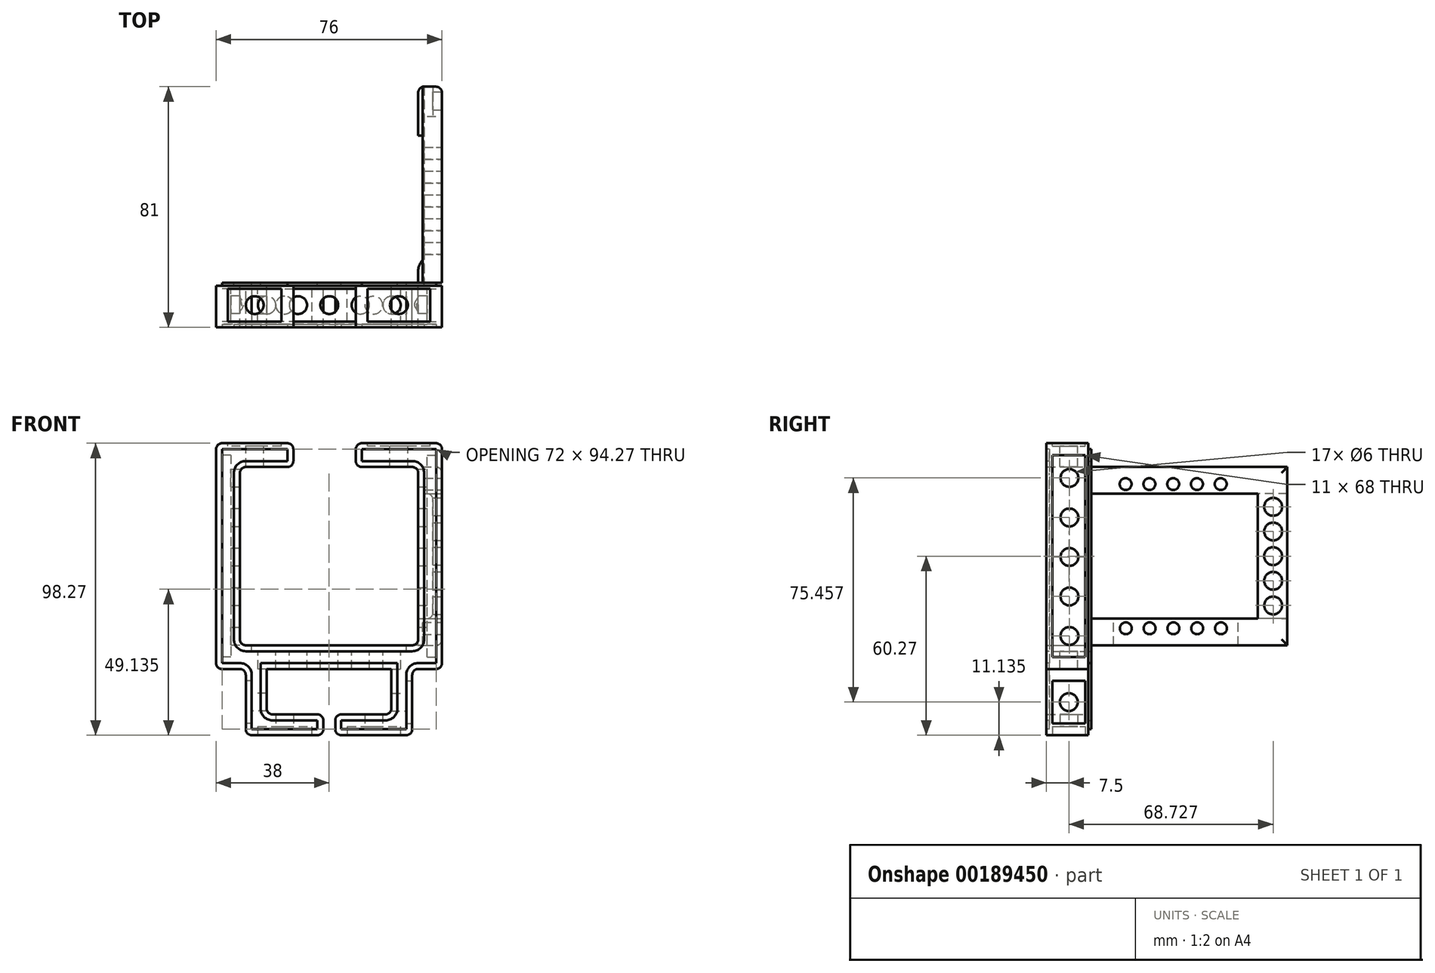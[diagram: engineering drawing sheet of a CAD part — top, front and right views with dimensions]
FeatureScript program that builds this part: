
annotation { "Feature Type Name" : "Feature", "Feature Type Description" : "" }
export const myFeature = defineFeature(function(context is Context, id is Id, definition is map)
    precondition{}
    {
        {
            var Q0;
            Q0=qCreatedBy(makeId("Front.planeOp"),FACE);
            var sketch = newSketch(context, id + "F0", { "sketchPlane" : qUnion([Q0])});
            skLineSegment(sketch, "E0.top", {"start": v(27.9, 40.9) * mm, "end": v(10.9, 40.9) * mm});
            skLineSegment(sketch, "E0.left", {"start": v(29.9, -17.1) * mm, "end": v(29.9, 38.9) * mm});
            skLineSegment(sketch, "E0.right", {"start": v(-30.1, -17.1) * mm, "end": v(-30.1, 38.9) * mm});
            skLineSegment(sketch, "E1.1", {"start": v(37.9, -25.1) * mm, "end": v(37.9, 46.9) * mm});
            skPoint(sketch, "E2.visualSharp", {"position": v(-30.1, -19.1) * mm});
            skArc(sketch, "E2.filletArc", {"start": v(-30.1, -17.1) * mm, "mid": v(-29.51, -18.51) * mm, "end": v(-28.1, -19.1) * mm});
            skPoint(sketch, "E3.visualSharp", {"position": v(29.9, -19.1) * mm});
            skArc(sketch, "E3.filletArc", {"start": v(27.9, -19.1) * mm, "mid": v(29.31, -18.51) * mm, "end": v(29.9, -17.1) * mm});
            skPoint(sketch, "E4.visualSharp", {"position": v(-30.1, 40.9) * mm});
            skArc(sketch, "E4.filletArc", {"start": v(-28.1, 40.9) * mm, "mid": v(-29.51, 40.31) * mm, "end": v(-30.1, 38.9) * mm});
            skPoint(sketch, "E5.visualSharp", {"position": v(29.9, 40.9) * mm});
            skArc(sketch, "E5.filletArc", {"start": v(29.9, 38.9) * mm, "mid": v(29.31, 40.31) * mm, "end": v(27.9, 40.9) * mm});
            skPoint(sketch, "E6.visualSharp", {"position": v(-38.1, 48.9) * mm});
            skArc(sketch, "E6.filletArc", {"start": v(-36.1, 48.9) * mm, "mid": v(-37.51, 48.31) * mm, "end": v(-38.1, 46.9) * mm});
            skPoint(sketch, "E7.visualSharp", {"position": v(37.9, 48.9) * mm});
            skArc(sketch, "E7.filletArc", {"start": v(37.9, 46.9) * mm, "mid": v(37.31, 48.31) * mm, "end": v(35.9, 48.9) * mm});
            skPoint(sketch, "E8.visualSharp", {"position": v(37.9, -27.1) * mm});
            skArc(sketch, "E8.filletArc", {"start": v(35.9, -27.1) * mm, "mid": v(37.31, -26.51) * mm, "end": v(37.9, -25.1) * mm});
            skPoint(sketch, "E9.visualSharp", {"position": v(-29.82, -12.89) * mm});
            skLineSegment(sketch, "E10", {"start": v(-28.1, -19.1) * mm, "end": v(27.9, -19.1) * mm});
            skLineSegment(sketch, "E11", {"start": v(-38.1, 46.9) * mm, "end": v(-38.1, -25.1) * mm});
            skLineSegment(sketch, "E12", {"start": v(-36.1, -27.1) * mm, "end": v(-30.1, -27.1) * mm});
            skLineSegment(sketch, "E13.bottom", {"start": v(-21.1, -27.1) * mm, "end": v(20.9, -27.1) * mm});
            skLineSegment(sketch, "E13.top", {"start": v(-26.1, -49.37) * mm, "end": v(-4, -49.37) * mm});
            skLineSegment(sketch, "E14", {"start": v(-28.1, -29.1) * mm, "end": v(-28.1, -47.37) * mm});
            skLineSegment(sketch, "E15", {"start": v(27.9, -47.37) * mm, "end": v(27.9, -29.1) * mm});
            skLineSegment(sketch, "E16", {"start": v(-19.1, -42.37) * mm, "end": v(-4, -42.37) * mm});
            skLineSegment(sketch, "E17", {"start": v(4, -42.37) * mm, "end": v(18.9, -42.37) * mm});
            skLineSegment(sketch, "E18", {"start": v(-2, -44.37) * mm, "end": v(-2, -47.37) * mm});
            skLineSegment(sketch, "E19", {"start": v(2, -44.37) * mm, "end": v(2, -47.37) * mm});
            skPoint(sketch, "E20.visualSharp", {"position": v(20.9, -42.37) * mm});
            skArc(sketch, "E20.filletArc", {"start": v(18.9, -42.37) * mm, "mid": v(20.31, -41.78) * mm, "end": v(20.9, -40.37) * mm});
            skPoint(sketch, "E21.visualSharp", {"position": v(-21.1, -42.37) * mm});
            skArc(sketch, "E21.filletArc", {"start": v(-21.1, -40.37) * mm, "mid": v(-20.51, -41.78) * mm, "end": v(-19.1, -42.37) * mm});
            skPoint(sketch, "E22.visualSharp", {"position": v(27.9, -49.37) * mm});
            skArc(sketch, "E22.filletArc", {"start": v(25.9, -49.37) * mm, "mid": v(27.31, -48.78) * mm, "end": v(27.9, -47.37) * mm});
            skPoint(sketch, "E23.visualSharp", {"position": v(-28.1, -49.37) * mm});
            skArc(sketch, "E23.filletArc", {"start": v(-28.1, -47.37) * mm, "mid": v(-27.51, -48.78) * mm, "end": v(-26.1, -49.37) * mm});
            skLineSegment(sketch, "E24.trimOffspring", {"start": v(29.9, -27.1) * mm, "end": v(35.9, -27.1) * mm});
            skPoint(sketch, "E25.visualSharp", {"position": v(27.9, -27.1) * mm});
            skArc(sketch, "E25.filletArc", {"start": v(29.9, -27.1) * mm, "mid": v(28.49, -27.69) * mm, "end": v(27.9, -29.1) * mm});
            skPoint(sketch, "E26.visualSharp", {"position": v(-28.1, -27.1) * mm});
            skArc(sketch, "E26.filletArc", {"start": v(-28.1, -29.1) * mm, "mid": v(-28.69, -27.69) * mm, "end": v(-30.1, -27.1) * mm});
            skPoint(sketch, "E27.visualSharp", {"position": v(-38.1, -27.1) * mm});
            skArc(sketch, "E27.filletArc", {"start": v(-38.1, -25.1) * mm, "mid": v(-37.51, -26.51) * mm, "end": v(-36.1, -27.1) * mm});
            skLineSegment(sketch, "E28", {"start": v(-21.1, -27.1) * mm, "end": v(-21.1, -40.37) * mm});
            skLineSegment(sketch, "E29", {"start": v(20.9, -27.1) * mm, "end": v(20.9, -40.37) * mm});
            skLineSegment(sketch, "E30.trimOffspring", {"start": v(4, -49.37) * mm, "end": v(25.9, -49.37) * mm});
            skPoint(sketch, "E31.start.orphan", {"position": v(0, -42.37) * mm});
            skPoint(sketch, "E32.visualSharp", {"position": v(-2, -42.37) * mm});
            skArc(sketch, "E32.filletArc", {"start": v(-2, -44.37) * mm, "mid": v(-2.59, -42.95) * mm, "end": v(-4, -42.37) * mm});
            skPoint(sketch, "E33.visualSharp", {"position": v(2, -42.37) * mm});
            skArc(sketch, "E33.filletArc", {"start": v(4, -42.37) * mm, "mid": v(2.59, -42.95) * mm, "end": v(2, -44.37) * mm});
            skPoint(sketch, "E34.visualSharp", {"position": v(2, -49.37) * mm});
            skArc(sketch, "E34.filletArc", {"start": v(2, -47.37) * mm, "mid": v(2.59, -48.78) * mm, "end": v(4, -49.37) * mm});
            skPoint(sketch, "E35.visualSharp", {"position": v(-2, -49.37) * mm});
            skArc(sketch, "E35.filletArc", {"start": v(-4, -49.37) * mm, "mid": v(-2.59, -48.78) * mm, "end": v(-2, -47.37) * mm});
            skLineSegment(sketch, "E36", {"start": v(27.9, -27.1) * mm, "end": v(27.9, -29.1) * mm});
            skLineSegment(sketch, "E37", {"start": v(-28.1, -19.1) * mm, "end": v(-28.1, -29.1) * mm});
            skLineSegment(sketch, "E38", {"start": v(29.9, -17.1) * mm, "end": v(29.9, -27.1) * mm});
            skLineSegment(sketch, "E39", {"start": v(-12.1, 46.9) * mm, "end": v(-12.1, 42.9) * mm});
            skLineSegment(sketch, "E40", {"start": v(8.9, 46.9) * mm, "end": v(8.9, 42.9) * mm});
            skLineSegment(sketch, "E41.trimOffspring", {"start": v(-14.1, 40.9) * mm, "end": v(-28.1, 40.9) * mm});
            skPoint(sketch, "E42.end.orphan", {"position": v(-0.1, 40.9) * mm});
            skPoint(sketch, "E43.orphan", {"position": v(-0.1, 48.9) * mm});
            skPoint(sketch, "E44.visualSharp", {"position": v(-12.1, 40.9) * mm});
            skArc(sketch, "E44.filletArc", {"start": v(-14.1, 40.9) * mm, "mid": v(-12.69, 41.49) * mm, "end": v(-12.1, 42.9) * mm});
            skPoint(sketch, "E45.visualSharp", {"position": v(8.9, 40.9) * mm});
            skArc(sketch, "E45.filletArc", {"start": v(8.9, 42.9) * mm, "mid": v(9.49, 41.49) * mm, "end": v(10.9, 40.9) * mm});
            skPoint(sketch, "E46.start.orphan", {"position": v(-18.1, 48.9) * mm});
            skPoint(sketch, "E47.start.orphan", {"position": v(17.9, 48.9) * mm});
            skLineSegment(sketch, "E48", {"start": v(-36.1, 48.9) * mm, "end": v(-14.1, 48.9) * mm});
            skLineSegment(sketch, "E49", {"start": v(10.9, 48.9) * mm, "end": v(35.9, 48.9) * mm});
            skPoint(sketch, "E50.visualSharp", {"position": v(-12.1, 48.9) * mm});
            skArc(sketch, "E50.filletArc", {"start": v(-12.1, 46.9) * mm, "mid": v(-12.69, 48.31) * mm, "end": v(-14.1, 48.9) * mm});
            skPoint(sketch, "E51.visualSharp", {"position": v(8.9, 48.9) * mm});
            skArc(sketch, "E51.filletArc", {"start": v(10.9, 48.9) * mm, "mid": v(9.49, 48.31) * mm, "end": v(8.9, 46.9) * mm});
            skSolve(sketch);
        }
        {
            var Q0;
            Q0=makeQuery(id+"F0.imprint","IMPRINT",FACE,{"disambiguationData":[TD([[makeQuery(id+"F0.imprint","IMPRINT",EDGE,{"derivedFrom":sQuery(id+"F0.wireOp",EDGE,"E0.left")}),-1.0]])]});
            var Q1;
            Q1=makeQuery(id+"F0.imprint","IMPRINT",FACE,{"disambiguationData":[TD([[makeQuery(id+"F0.imprint","IMPRINT",EDGE,{"derivedFrom":sQuery(id+"F0.wireOp",EDGE,"E0.right")}),1.0]])]});
            var Q2;
            Q2=makeQuery(id+"F0.imprint","IMPRINT",FACE,{"disambiguationData":[TD([[makeQuery(id+"F0.imprint","IMPRINT",EDGE,{"derivedFrom":sQuery(id+"F0.wireOp",EDGE,"E10")}),-1.0]])]});
            var Q3;
            {var subQ0=sQuery(id+"F0.wireOp",EDGE,"iEe1PrU2-Olpx-yFy5-rcaY-dY1r3bGIUNjf");Q3=makeQuery(id+"F0.imprint","IMPRINT",FACE,{"disambiguationData":[TD([[makeQuery(id+"F0.imprint","IMPRINT",EDGE,{"derivedFrom":subQ0}),1.0]])]});}
            var Q4;
            {var subQ0=sQuery(id+"F0.wireOp",EDGE,"4XO8oygt-JLlM-bsj2-xD9l-5jJy744JPbBX");Q4=makeQuery(id+"F0.imprint","IMPRINT",FACE,{"disambiguationData":[TD([[makeQuery(id+"F0.imprint","IMPRINT",EDGE,{"derivedFrom":subQ0}),-1.0]])]});}
            extrude(context, id + "F1", {"entities" : qUnion([Q0, Q1, Q2, Q3, Q4]), "depth" : 15 * mm});
        }
        {
            var Q0;
            Q0=makeQuery(id+"F1.opExtrude","SWEPT_FACE",FACE,{"disambiguationData":[OSD([sQuery(id+"F0.wireOp",EDGE,"E11")])]});
            var sketch = newSketch(context, id + "F2", { "sketchPlane" : qUnion([Q0])});
            skLineSegment(sketch, "E52.0", {"start": v(2, 44.9) * mm, "end": v(2, -23.1) * mm});
            skLineSegment(sketch, "E52.1", {"start": v(13, 44.9) * mm, "end": v(2, 44.9) * mm});
            skLineSegment(sketch, "E52.2", {"start": v(13, -23.1) * mm, "end": v(13, 44.9) * mm});
            skLineSegment(sketch, "E52.3", {"start": v(2, -23.1) * mm, "end": v(13, -23.1) * mm});
            skSolve(sketch);
        }
        {
            var Q0;
            Q0=makeQuery(id+"F2.imprint","IMPRINT",FACE,{"disambiguationData":[TD([[makeQuery(id+"F2.imprint","IMPRINT",EDGE,{"derivedFrom":sQuery(id+"F2.wireOp",EDGE,"E52.0")}),1.0]])]});
            extrude(context, id + "F3", {"entities" : qUnion([Q0]), "operationType" : NewBodyOperationType.REMOVE, "oppositeDirection" : true, "depth" : 5 * mm});
        }
        {
            var Q0;
            Q0=makeQuery(id+"F1.opExtrude","SWEPT_FACE",FACE,{"disambiguationData":[OSD([sQuery(id+"F0.wireOp",EDGE,"E1.1")])]});
            var sketch = newSketch(context, id + "F4", { "sketchPlane" : qUnion([Q0])});
            skLineSegment(sketch, "E53.0", {"start": v(-2, -23.1) * mm, "end": v(-2, 44.9) * mm});
            skLineSegment(sketch, "E53.1", {"start": v(-13, -23.1) * mm, "end": v(-2, -23.1) * mm});
            skLineSegment(sketch, "E53.2", {"start": v(-13, 44.9) * mm, "end": v(-13, -23.1) * mm});
            skLineSegment(sketch, "E53.3", {"start": v(-2, 44.9) * mm, "end": v(-13, 44.9) * mm});
            skCircle(sketch, "E54", {"center": v(-7.3, 37.22) * mm, "radius": 3 * mm});
            skCircle(sketch, "E55.0.1.0", {"center": v(-7.3, 23.92) * mm, "radius": 3 * mm});
            skCircle(sketch, "E55.0.2.0", {"center": v(-7.3, 10.62) * mm, "radius": 3 * mm});
            skCircle(sketch, "E55.0.3.0", {"center": v(-7.3, -2.68) * mm, "radius": 3 * mm});
            skCircle(sketch, "E55.0.4.0", {"center": v(-7.3, -15.98) * mm, "radius": 3 * mm});
            skLineSegment(sketch, "E55.direction1", {"start": v(-7.8, 37.22) * mm, "end": v(17.2, 37.22) * mm, "construction": true});
            skLineSegment(sketch, "E55.direction2", {"start": v(-7.8, 37.22) * mm, "end": v(-7.8, 23.92) * mm, "construction": true});
            skSolve(sketch);
        }
        {
            var Q0;
            Q0=makeQuery(id+"F4.imprint","IMPRINT",FACE,{"disambiguationData":[TD([[makeQuery(id+"F4.imprint","IMPRINT",EDGE,{"derivedFrom":sQuery(id+"F4.wireOp",EDGE,"E54")}),1.0]])]});
            var Q1;
            Q1=makeQuery(id+"F4.imprint","IMPRINT",FACE,{"disambiguationData":[TD([[makeQuery(id+"F4.imprint","IMPRINT",EDGE,{"derivedFrom":sQuery(id+"F4.wireOp",EDGE,"E55.0.1.0")}),1.0]])]});
            var Q2;
            Q2=makeQuery(id+"F4.imprint","IMPRINT",FACE,{"disambiguationData":[TD([[makeQuery(id+"F4.imprint","IMPRINT",EDGE,{"derivedFrom":sQuery(id+"F4.wireOp",EDGE,"E55.0.2.0")}),1.0]])]});
            var Q3;
            Q3=makeQuery(id+"F4.imprint","IMPRINT",FACE,{"disambiguationData":[TD([[makeQuery(id+"F4.imprint","IMPRINT",EDGE,{"derivedFrom":sQuery(id+"F4.wireOp",EDGE,"E55.0.3.0")}),1.0]])]});
            var Q4;
            Q4=makeQuery(id+"F4.imprint","IMPRINT",FACE,{"disambiguationData":[TD([[makeQuery(id+"F4.imprint","IMPRINT",EDGE,{"derivedFrom":sQuery(id+"F4.wireOp",EDGE,"E55.0.4.0")}),1.0]])]});
            extrude(context, id + "F5", {"entities" : qUnion([Q0, Q1, Q2, Q3, Q4]), "operationType" : NewBodyOperationType.REMOVE, "oppositeDirection" : true, "depth" : 90.3 * mm});
        }
        {
            var Q0;
            Q0=makeQuery(id+"F4.imprint","IMPRINT",FACE,{"disambiguationData":[TD([[makeQuery(id+"F4.imprint","IMPRINT",EDGE,{"derivedFrom":sQuery(id+"F4.wireOp",EDGE,"E53.0")}),1.0]])]});
            extrude(context, id + "F6", {"entities" : qUnion([Q0]), "operationType" : NewBodyOperationType.REMOVE, "oppositeDirection" : true, "depth" : 5 * mm});
        }
        {
            var Q0;
            Q0=makeQuery(id+"F1.opExtrude","CAP_FACE",FACE,{"disambiguationData":[OSD([sQuery(id+"F0.wireOp",EDGE,"E0.top"),sQuery(id+"F0.wireOp",EDGE,"E0.left"),sQuery(id+"F0.wireOp",EDGE,"E0.right"),sQuery(id+"F0.wireOp",EDGE,"E1.0"),sQuery(id+"F0.wireOp",EDGE,"E1.1"),sQuery(id+"F0.wireOp",EDGE,"E2.filletArc"),sQuery(id+"F0.wireOp",EDGE,"E3.filletArc"),sQuery(id+"F0.wireOp",EDGE,"E4.filletArc"),sQuery(id+"F0.wireOp",EDGE,"E5.filletArc"),sQuery(id+"F0.wireOp",EDGE,"E6.filletArc"),sQuery(id+"F0.wireOp",EDGE,"E7.filletArc"),sQuery(id+"F0.wireOp",EDGE,"E8.filletArc"),sQuery(id+"F0.wireOp",EDGE,"XpEmfxVq-F5ly-u82n-WrmS-VlENYUEvmkYp"),sQuery(id+"F0.wireOp",EDGE,"E10"),sQuery(id+"F0.wireOp",EDGE,"E11"),sQuery(id+"F0.wireOp",EDGE,"E12"),sQuery(id+"F0.wireOp",EDGE,"E13.top"),sQuery(id+"F0.wireOp",EDGE,"E14"),sQuery(id+"F0.wireOp",EDGE,"E15"),sQuery(id+"F0.wireOp",EDGE,"E16"),sQuery(id+"F0.wireOp",EDGE,"E17"),sQuery(id+"F0.wireOp",EDGE,"E18"),sQuery(id+"F0.wireOp",EDGE,"E19"),sQuery(id+"F0.wireOp",EDGE,"E20.filletArc"),sQuery(id+"F0.wireOp",EDGE,"E21.filletArc"),sQuery(id+"F0.wireOp",EDGE,"E22.filletArc"),sQuery(id+"F0.wireOp",EDGE,"E23.filletArc"),sQuery(id+"F0.wireOp",EDGE,"E13.bottom"),sQuery(id+"F0.wireOp",EDGE,"E24.trimOffspring"),sQuery(id+"F0.wireOp",EDGE,"E25.filletArc"),sQuery(id+"F0.wireOp",EDGE,"E26.filletArc"),sQuery(id+"F0.wireOp",EDGE,"E27.filletArc"),sQuery(id+"F0.wireOp",EDGE,"E28"),sQuery(id+"F0.wireOp",EDGE,"E29"),sQuery(id+"F0.wireOp",EDGE,"E30.trimOffspring"),sQuery(id+"F0.wireOp",EDGE,"E32.filletArc"),sQuery(id+"F0.wireOp",EDGE,"E33.filletArc"),sQuery(id+"F0.wireOp",EDGE,"E34.filletArc"),sQuery(id+"F0.wireOp",EDGE,"E35.filletArc"),sQuery(id+"F0.wireOp",EDGE,"E46"),sQuery(id+"F0.wireOp",EDGE,"E47"),sQuery(id+"F0.wireOp",EDGE,"E39"),sQuery(id+"F0.wireOp",EDGE,"E40")])],"isStart":false});
            var sketch = newSketch(context, id + "F7", { "sketchPlane" : qUnion([Q0])});
            skLineSegment(sketch, "E56.0", {"start": v(10.9, 46.9) * mm, "end": v(10.9, 42.9) * mm});
            skLineSegment(sketch, "E56.1", {"start": v(35.9, 46.9) * mm, "end": v(10.9, 46.9) * mm});
            skLineSegment(sketch, "E56.2", {"start": v(35.9, -25.1) * mm, "end": v(35.9, 46.9) * mm});
            skLineSegment(sketch, "E56.3", {"start": v(29.9, -25.1) * mm, "end": v(35.9, -25.1) * mm});
            skArc(sketch, "E56.4", {"start": v(25.9, -29.1) * mm, "mid": v(27.07, -26.27) * mm, "end": v(29.9, -25.1) * mm});
            skLineSegment(sketch, "E56.5", {"start": v(25.9, -47.37) * mm, "end": v(25.9, -29.1) * mm});
            skLineSegment(sketch, "E56.6", {"start": v(4, -47.37) * mm, "end": v(25.9, -47.37) * mm});
            skLineSegment(sketch, "E56.7", {"start": v(4, -44.37) * mm, "end": v(4, -47.37) * mm});
            skLineSegment(sketch, "E56.8", {"start": v(18.9, -44.37) * mm, "end": v(4, -44.37) * mm});
            skLineSegment(sketch, "E56.9", {"start": v(-14.1, 46.9) * mm, "end": v(-36.1, 46.9) * mm});
            skLineSegment(sketch, "E56.10", {"start": v(-14.1, 42.9) * mm, "end": v(-14.1, 46.9) * mm});
            skLineSegment(sketch, "E56.11", {"start": v(-28.1, 42.9) * mm, "end": v(-14.1, 42.9) * mm});
            skArc(sketch, "E56.12", {"start": v(-32.1, 38.9) * mm, "mid": v(-30.93, 41.73) * mm, "end": v(-28.1, 42.9) * mm});
            skLineSegment(sketch, "E56.13", {"start": v(-32.1, -17.1) * mm, "end": v(-32.1, 38.9) * mm});
            skArc(sketch, "E56.14", {"start": v(-28.1, -21.1) * mm, "mid": v(-30.93, -19.93) * mm, "end": v(-32.1, -17.1) * mm});
            skArc(sketch, "E56.15", {"start": v(27.9, 42.9) * mm, "mid": v(30.73, 41.73) * mm, "end": v(31.9, 38.9) * mm});
            skLineSegment(sketch, "E56.16", {"start": v(31.9, 38.9) * mm, "end": v(31.9, -17.1) * mm});
            skArc(sketch, "E56.17", {"start": v(31.9, -17.1) * mm, "mid": v(30.73, -19.93) * mm, "end": v(27.9, -21.1) * mm});
            skLineSegment(sketch, "E56.18", {"start": v(27.9, -21.1) * mm, "end": v(-28.1, -21.1) * mm});
            skLineSegment(sketch, "E56.19", {"start": v(-36.1, 46.9) * mm, "end": v(-36.1, -25.1) * mm});
            skLineSegment(sketch, "E56.20", {"start": v(-36.1, -25.1) * mm, "end": v(-30.1, -25.1) * mm});
            skArc(sketch, "E56.21", {"start": v(-30.1, -25.1) * mm, "mid": v(-27.27, -26.27) * mm, "end": v(-26.1, -29.1) * mm});
            skLineSegment(sketch, "E56.22", {"start": v(-26.1, -29.1) * mm, "end": v(-26.1, -47.37) * mm});
            skLineSegment(sketch, "E56.23", {"start": v(-26.1, -47.37) * mm, "end": v(-4, -47.37) * mm});
            skLineSegment(sketch, "E56.24", {"start": v(-4, -47.37) * mm, "end": v(-4, -44.37) * mm});
            skLineSegment(sketch, "E56.25", {"start": v(-4, -44.37) * mm, "end": v(-19.1, -44.37) * mm});
            skArc(sketch, "E56.26", {"start": v(-19.1, -44.37) * mm, "mid": v(-21.93, -43.2) * mm, "end": v(-23.1, -40.37) * mm});
            skLineSegment(sketch, "E56.27", {"start": v(-23.1, -40.37) * mm, "end": v(-23.1, -25.1) * mm});
            skLineSegment(sketch, "E56.28", {"start": v(10.9, 42.9) * mm, "end": v(27.9, 42.9) * mm});
            skLineSegment(sketch, "E56.29", {"start": v(-23.1, -25.1) * mm, "end": v(22.9, -25.1) * mm});
            skLineSegment(sketch, "E56.30", {"start": v(22.9, -25.1) * mm, "end": v(22.9, -40.37) * mm});
            skArc(sketch, "E56.31", {"start": v(22.9, -40.37) * mm, "mid": v(21.73, -43.2) * mm, "end": v(18.9, -44.37) * mm});
            skSolve(sketch);
        }
        {
            var Q0;
            Q0=makeQuery(id+"F7.imprint","IMPRINT",FACE,{"disambiguationData":[TD([[makeQuery(id+"F7.imprint","IMPRINT",EDGE,{"derivedFrom":sQuery(id+"F7.wireOp",EDGE,"E56.0")}),1.0]])]});
            extrude(context, id + "F8", {"entities" : qUnion([Q0]), "operationType" : NewBodyOperationType.REMOVE, "oppositeDirection" : true, "depth" : 1 * mm});
        }
        {
            var Q0;
            Q0=makeQuery(id+"F1.opExtrude","CAP_FACE",FACE,{"disambiguationData":[OSD([sQuery(id+"F0.wireOp",EDGE,"E0.top"),sQuery(id+"F0.wireOp",EDGE,"E0.left"),sQuery(id+"F0.wireOp",EDGE,"E0.right"),sQuery(id+"F0.wireOp",EDGE,"E1.0"),sQuery(id+"F0.wireOp",EDGE,"E1.1"),sQuery(id+"F0.wireOp",EDGE,"E2.filletArc"),sQuery(id+"F0.wireOp",EDGE,"E3.filletArc"),sQuery(id+"F0.wireOp",EDGE,"E4.filletArc"),sQuery(id+"F0.wireOp",EDGE,"E5.filletArc"),sQuery(id+"F0.wireOp",EDGE,"E6.filletArc"),sQuery(id+"F0.wireOp",EDGE,"E7.filletArc"),sQuery(id+"F0.wireOp",EDGE,"E8.filletArc"),sQuery(id+"F0.wireOp",EDGE,"XpEmfxVq-F5ly-u82n-WrmS-VlENYUEvmkYp"),sQuery(id+"F0.wireOp",EDGE,"E10"),sQuery(id+"F0.wireOp",EDGE,"E11"),sQuery(id+"F0.wireOp",EDGE,"E12"),sQuery(id+"F0.wireOp",EDGE,"E13.top"),sQuery(id+"F0.wireOp",EDGE,"E14"),sQuery(id+"F0.wireOp",EDGE,"E15"),sQuery(id+"F0.wireOp",EDGE,"E16"),sQuery(id+"F0.wireOp",EDGE,"E17"),sQuery(id+"F0.wireOp",EDGE,"E18"),sQuery(id+"F0.wireOp",EDGE,"E19"),sQuery(id+"F0.wireOp",EDGE,"E20.filletArc"),sQuery(id+"F0.wireOp",EDGE,"E21.filletArc"),sQuery(id+"F0.wireOp",EDGE,"E22.filletArc"),sQuery(id+"F0.wireOp",EDGE,"E23.filletArc"),sQuery(id+"F0.wireOp",EDGE,"E13.bottom"),sQuery(id+"F0.wireOp",EDGE,"E24.trimOffspring"),sQuery(id+"F0.wireOp",EDGE,"E25.filletArc"),sQuery(id+"F0.wireOp",EDGE,"E26.filletArc"),sQuery(id+"F0.wireOp",EDGE,"E27.filletArc"),sQuery(id+"F0.wireOp",EDGE,"E28"),sQuery(id+"F0.wireOp",EDGE,"E29"),sQuery(id+"F0.wireOp",EDGE,"E30.trimOffspring"),sQuery(id+"F0.wireOp",EDGE,"E32.filletArc"),sQuery(id+"F0.wireOp",EDGE,"E33.filletArc"),sQuery(id+"F0.wireOp",EDGE,"E34.filletArc"),sQuery(id+"F0.wireOp",EDGE,"E35.filletArc"),sQuery(id+"F0.wireOp",EDGE,"E46"),sQuery(id+"F0.wireOp",EDGE,"E47"),sQuery(id+"F0.wireOp",EDGE,"E39"),sQuery(id+"F0.wireOp",EDGE,"E40")])],"isStart":true});
            var sketch = newSketch(context, id + "F9", { "sketchPlane" : qUnion([Q0])});
            skArc(sketch, "E57.0", {"start": v(-31.9, 38.9) * mm, "mid": v(-30.73, 41.73) * mm, "end": v(-27.9, 42.9) * mm});
            skLineSegment(sketch, "E57.1", {"start": v(-31.9, -17.1) * mm, "end": v(-31.9, 38.9) * mm});
            skArc(sketch, "E57.2", {"start": v(-27.9, -21.1) * mm, "mid": v(-30.73, -19.93) * mm, "end": v(-31.9, -17.1) * mm});
            skLineSegment(sketch, "E57.3", {"start": v(28.1, -21.1) * mm, "end": v(-27.9, -21.1) * mm});
            skArc(sketch, "E57.4", {"start": v(32.1, -17.1) * mm, "mid": v(30.93, -19.93) * mm, "end": v(28.1, -21.1) * mm});
            skLineSegment(sketch, "E57.5", {"start": v(32.1, 38.9) * mm, "end": v(32.1, -17.1) * mm});
            skArc(sketch, "E57.6", {"start": v(28.1, 42.9) * mm, "mid": v(30.93, 41.73) * mm, "end": v(32.1, 38.9) * mm});
            skLineSegment(sketch, "E57.7", {"start": v(14.1, 42.9) * mm, "end": v(28.1, 42.9) * mm});
            skLineSegment(sketch, "E57.8", {"start": v(14.1, 46.9) * mm, "end": v(14.1, 42.9) * mm});
            skArc(sketch, "E57.9", {"start": v(-18.9, -44.37) * mm, "mid": v(-21.73, -43.2) * mm, "end": v(-22.9, -40.37) * mm});
            skLineSegment(sketch, "E57.10", {"start": v(-4, -44.37) * mm, "end": v(-18.9, -44.37) * mm});
            skLineSegment(sketch, "E57.11", {"start": v(-4, -47.37) * mm, "end": v(-4, -44.37) * mm});
            skLineSegment(sketch, "E57.12", {"start": v(-25.9, -47.37) * mm, "end": v(-4, -47.37) * mm});
            skLineSegment(sketch, "E57.13", {"start": v(-25.9, -29.1) * mm, "end": v(-25.9, -47.37) * mm});
            skArc(sketch, "E57.14", {"start": v(-29.9, -25.1) * mm, "mid": v(-27.07, -26.27) * mm, "end": v(-25.9, -29.1) * mm});
            skLineSegment(sketch, "E57.15", {"start": v(-10.9, 42.9) * mm, "end": v(-10.9, 46.9) * mm});
            skLineSegment(sketch, "E57.16", {"start": v(-10.9, 46.9) * mm, "end": v(-35.9, 46.9) * mm});
            skLineSegment(sketch, "E57.17", {"start": v(-35.9, 46.9) * mm, "end": v(-35.9, -25.1) * mm});
            skLineSegment(sketch, "E57.18", {"start": v(-35.9, -25.1) * mm, "end": v(-29.9, -25.1) * mm});
            skLineSegment(sketch, "E57.19", {"start": v(-22.9, -40.37) * mm, "end": v(-22.9, -25.1) * mm});
            skLineSegment(sketch, "E57.20", {"start": v(-22.9, -25.1) * mm, "end": v(23.1, -25.1) * mm});
            skLineSegment(sketch, "E57.21", {"start": v(23.1, -25.1) * mm, "end": v(23.1, -40.37) * mm});
            skArc(sketch, "E57.22", {"start": v(23.1, -40.37) * mm, "mid": v(21.93, -43.2) * mm, "end": v(19.1, -44.37) * mm});
            skLineSegment(sketch, "E57.23", {"start": v(19.1, -44.37) * mm, "end": v(4, -44.37) * mm});
            skLineSegment(sketch, "E57.24", {"start": v(4, -44.37) * mm, "end": v(4, -47.37) * mm});
            skLineSegment(sketch, "E57.25", {"start": v(4, -47.37) * mm, "end": v(26.1, -47.37) * mm});
            skLineSegment(sketch, "E57.26", {"start": v(26.1, -47.37) * mm, "end": v(26.1, -29.1) * mm});
            skArc(sketch, "E57.27", {"start": v(26.1, -29.1) * mm, "mid": v(27.27, -26.27) * mm, "end": v(30.1, -25.1) * mm});
            skLineSegment(sketch, "E57.28", {"start": v(-27.9, 42.9) * mm, "end": v(-10.9, 42.9) * mm});
            skLineSegment(sketch, "E57.29", {"start": v(30.1, -25.1) * mm, "end": v(36.1, -25.1) * mm});
            skLineSegment(sketch, "E57.30", {"start": v(36.1, -25.1) * mm, "end": v(36.1, 46.9) * mm});
            skLineSegment(sketch, "E57.31", {"start": v(36.1, 46.9) * mm, "end": v(14.1, 46.9) * mm});
            skSolve(sketch);
        }
        {
            var Q0;
            Q0=makeQuery(id+"F9.imprint","IMPRINT",FACE,{"disambiguationData":[TD([[makeQuery(id+"F9.imprint","IMPRINT",EDGE,{"derivedFrom":sQuery(id+"F9.wireOp",EDGE,"E57.0")}),1.0]])]});
            extrude(context, id + "F10", {"entities" : qUnion([Q0]), "operationType" : NewBodyOperationType.REMOVE, "oppositeDirection" : true, "depth" : 1 * mm});
        }
        {
            var Q0;
            Q0=makeQuery(id+"F1.opExtrude","SWEPT_FACE",FACE,{"disambiguationData":[OSD([sQuery(id+"F0.wireOp",EDGE,"E10")])]});
            var sketch = newSketch(context, id + "F11", { "sketchPlane" : qUnion([Q0])});
            skLineSegment(sketch, "E58.0", {"start": v(25.9, -2) * mm, "end": v(-26.1, -2) * mm});
            skLineSegment(sketch, "E58.1", {"start": v(25.9, -13) * mm, "end": v(25.9, -2) * mm});
            skLineSegment(sketch, "E58.2", {"start": v(-26.1, -13) * mm, "end": v(25.9, -13) * mm});
            skLineSegment(sketch, "E58.3", {"start": v(-26.1, -2) * mm, "end": v(-26.1, -13) * mm});
            skCircle(sketch, "E59", {"center": v(0, -7.5) * mm, "radius": 3 * mm});
            skPoint(sketch, "E59.centerSnap0", {"position": v(25.9, -7.5) * mm});
            skCircle(sketch, "E60", {"center": v(-26.1, -46.3) * mm, "radius": 6.5 * mm});
            skPoint(sketch, "E60.centerSnap0", {"position": v(-26.1, -7.5) * mm});
            skCircle(sketch, "E61.1.0.0", {"center": v(10.5, -7.5) * mm, "radius": 3 * mm});
            skCircle(sketch, "E61.2.0.0", {"center": v(21, -7.5) * mm, "radius": 3 * mm});
            skLineSegment(sketch, "E61.direction1", {"start": v(0, -7.5) * mm, "end": v(10.5, -7.5) * mm, "construction": true});
            skCircle(sketch, "E62.1.0.0", {"center": v(-10.5, -7.5) * mm, "radius": 3 * mm});
            skCircle(sketch, "E62.2.0.0", {"center": v(-21, -7.5) * mm, "radius": 3 * mm});
            skLineSegment(sketch, "E62.direction1", {"start": v(0, -7.5) * mm, "end": v(-10.5, -7.5) * mm, "construction": true});
            skSolve(sketch);
        }
        {
            var Q0;
            Q0=makeQuery(id+"F11.imprint","IMPRINT",FACE,{"disambiguationData":[TD([[makeQuery(id+"F11.imprint","IMPRINT",EDGE,{"derivedFrom":sQuery(id+"F11.wireOp",EDGE,"E61.2.0.0")}),1.0]])]});
            var Q1;
            Q1=makeQuery(id+"F11.imprint","IMPRINT",FACE,{"disambiguationData":[TD([[makeQuery(id+"F11.imprint","IMPRINT",EDGE,{"derivedFrom":sQuery(id+"F11.wireOp",EDGE,"E61.1.0.0")}),1.0]])]});
            var Q2;
            Q2=makeQuery(id+"F11.imprint","IMPRINT",FACE,{"disambiguationData":[TD([[makeQuery(id+"F11.imprint","IMPRINT",EDGE,{"derivedFrom":sQuery(id+"F11.wireOp",EDGE,"E59")}),1.0]])]});
            var Q3;
            Q3=makeQuery(id+"F11.imprint","IMPRINT",FACE,{"disambiguationData":[TD([[makeQuery(id+"F11.imprint","IMPRINT",EDGE,{"derivedFrom":sQuery(id+"F11.wireOp",EDGE,"E62.1.0.0")}),1.0]])]});
            var Q4;
            Q4=makeQuery(id+"F11.imprint","IMPRINT",FACE,{"disambiguationData":[TD([[makeQuery(id+"F11.imprint","IMPRINT",EDGE,{"derivedFrom":sQuery(id+"F11.wireOp",EDGE,"E62.2.0.0")}),1.0]])]});
            extrude(context, id + "F12", {"entities" : qUnion([Q0, Q1, Q2, Q3, Q4]), "operationType" : NewBodyOperationType.REMOVE, "oppositeDirection" : true, "depth" : 8 * mm});
        }
        {
            var Q0;
            Q0=makeQuery(id+"F11.imprint","IMPRINT",FACE,{"disambiguationData":[TD([[makeQuery(id+"F11.imprint","IMPRINT",EDGE,{"derivedFrom":sQuery(id+"F11.wireOp",EDGE,"E58.0")}),1.0]])]});
            extrude(context, id + "F13", {"entities" : qUnion([Q0]), "operationType" : NewBodyOperationType.REMOVE, "oppositeDirection" : true, "depth" : 2 * mm});
        }
        {
            var Q0;
            Q0=makeQuery(id+"F1.opExtrude","SWEPT_FACE",FACE,{"disambiguationData":[OSD([sQuery(id+"F0.wireOp",EDGE,"E15")])]});
            var sketch = newSketch(context, id + "F14", { "sketchPlane" : qUnion([Q0])});
            skLineSegment(sketch, "E63.0", {"start": v(-2, -45.37) * mm, "end": v(-2, -31.1) * mm});
            skLineSegment(sketch, "E63.1", {"start": v(-13, -45.37) * mm, "end": v(-2, -45.37) * mm});
            skLineSegment(sketch, "E63.2", {"start": v(-13, -31.1) * mm, "end": v(-13, -45.37) * mm});
            skLineSegment(sketch, "E63.3", {"start": v(-2, -31.1) * mm, "end": v(-13, -31.1) * mm});
            skCircle(sketch, "E64", {"center": v(-7.5, -38.23) * mm, "radius": 3 * mm});
            skPoint(sketch, "E64.centerSnap0", {"position": v(-13, -38.23) * mm});
            skPoint(sketch, "E64.centerSnap1", {"position": v(-7.5, -31.1) * mm});
            skSolve(sketch);
        }
        {
            var Q0;
            Q0=makeQuery(id+"F14.imprint","IMPRINT",FACE,{"disambiguationData":[TD([[makeQuery(id+"F14.imprint","IMPRINT",EDGE,{"derivedFrom":sQuery(id+"F14.wireOp",EDGE,"E64")}),1.0]])]});
            extrude(context, id + "F15", {"entities" : qUnion([Q0]), "operationType" : NewBodyOperationType.REMOVE, "oppositeDirection" : true, "depth" : 8 * mm});
        }
        {
            var Q0;
            Q0=makeQuery(id+"F14.imprint","IMPRINT",FACE,{"disambiguationData":[TD([[makeQuery(id+"F14.imprint","IMPRINT",EDGE,{"derivedFrom":sQuery(id+"F14.wireOp",EDGE,"E63.0")}),1.0]])]});
            extrude(context, id + "F16", {"entities" : qUnion([Q0]), "operationType" : NewBodyOperationType.REMOVE, "oppositeDirection" : true, "depth" : 2 * mm});
        }
        {
            var Q0;
            Q0=makeQuery(id+"F1.opExtrude","SWEPT_FACE",FACE,{"disambiguationData":[OSD([sQuery(id+"F0.wireOp",EDGE,"E14")])]});
            var sketch = newSketch(context, id + "F17", { "sketchPlane" : qUnion([Q0])});
            skLineSegment(sketch, "E65.0", {"start": v(2, -31.1) * mm, "end": v(2, -45.37) * mm});
            skLineSegment(sketch, "E65.1", {"start": v(13, -31.1) * mm, "end": v(2, -31.1) * mm});
            skLineSegment(sketch, "E65.2", {"start": v(13, -45.37) * mm, "end": v(13, -31.1) * mm});
            skLineSegment(sketch, "E65.3", {"start": v(2, -45.37) * mm, "end": v(13, -45.37) * mm});
            skCircle(sketch, "E66", {"center": v(7.5, -38.23) * mm, "radius": 3 * mm});
            skPoint(sketch, "E66.centerSnap0", {"position": v(2, -38.23) * mm});
            skPoint(sketch, "E66.centerSnap1", {"position": v(7.5, -31.1) * mm});
            skSolve(sketch);
        }
        {
            var Q0;
            Q0=makeQuery(id+"F17.imprint","IMPRINT",FACE,{"disambiguationData":[TD([[makeQuery(id+"F17.imprint","IMPRINT",EDGE,{"derivedFrom":sQuery(id+"F17.wireOp",EDGE,"E66")}),1.0]])]});
            extrude(context, id + "F18", {"entities" : qUnion([Q0]), "operationType" : NewBodyOperationType.REMOVE, "oppositeDirection" : true, "depth" : 8 * mm});
        }
        {
            var Q0;
            Q0=makeQuery(id+"F17.imprint","IMPRINT",FACE,{"disambiguationData":[TD([[makeQuery(id+"F17.imprint","IMPRINT",EDGE,{"derivedFrom":sQuery(id+"F17.wireOp",EDGE,"E65.0")}),1.0]])]});
            extrude(context, id + "F19", {"entities" : qUnion([Q0]), "operationType" : NewBodyOperationType.REMOVE, "oppositeDirection" : true, "depth" : 2 * mm});
        }
        {
            var Q0;
            Q0=makeQuery(id+"F1.opExtrude","SWEPT_FACE",FACE,{"disambiguationData":[OSD([sQuery(id+"F0.wireOp",EDGE,"E13.top")])]});
            var sketch = newSketch(context, id + "F20", { "sketchPlane" : qUnion([Q0])});
            skLineSegment(sketch, "E67.0", {"start": v(-24.1, 2) * mm, "end": v(-6, 2) * mm});
            skLineSegment(sketch, "E67.1", {"start": v(-24.1, 13) * mm, "end": v(-24.1, 2) * mm});
            skLineSegment(sketch, "E67.2", {"start": v(-6, 13) * mm, "end": v(-24.1, 13) * mm});
            skLineSegment(sketch, "E67.3", {"start": v(-6, 2) * mm, "end": v(-6, 13) * mm});
            skLineSegment(sketch, "E68.0", {"start": v(6, 2) * mm, "end": v(23.9, 2) * mm});
            skLineSegment(sketch, "E68.1", {"start": v(6, 13) * mm, "end": v(6, 2) * mm});
            skLineSegment(sketch, "E68.2", {"start": v(23.9, 13) * mm, "end": v(6, 13) * mm});
            skLineSegment(sketch, "E68.3", {"start": v(23.9, 2) * mm, "end": v(23.9, 13) * mm});
            skCircle(sketch, "E69", {"center": v(-15.05, 7.5) * mm, "radius": 3 * mm});
            skPoint(sketch, "E69.centerSnap0", {"position": v(-24.1, 7.5) * mm});
            skPoint(sketch, "E69.centerSnap1", {"position": v(-15.05, 13) * mm});
            skCircle(sketch, "E70", {"center": v(14.95, 7.5) * mm, "radius": 3 * mm});
            skPoint(sketch, "E70.centerSnap0", {"position": v(6, 7.5) * mm});
            skPoint(sketch, "E70.centerSnap1", {"position": v(14.95, 13) * mm});
            skSolve(sketch);
        }
        {
            var Q0;
            Q0=makeQuery(id+"F20.imprint","IMPRINT",FACE,{"disambiguationData":[TD([[makeQuery(id+"F20.imprint","IMPRINT",EDGE,{"derivedFrom":sQuery(id+"F20.wireOp",EDGE,"E69")}),1.0]])]});
            var Q1;
            Q1=makeQuery(id+"F20.imprint","IMPRINT",FACE,{"disambiguationData":[TD([[makeQuery(id+"F20.imprint","IMPRINT",EDGE,{"derivedFrom":sQuery(id+"F20.wireOp",EDGE,"E70")}),1.0]])]});
            extrude(context, id + "F21", {"entities" : qUnion([Q0, Q1]), "operationType" : NewBodyOperationType.REMOVE, "oppositeDirection" : true, "depth" : 8 * mm});
        }
        {
            var Q0;
            Q0=makeQuery(id+"F20.imprint","IMPRINT",FACE,{"disambiguationData":[TD([[makeQuery(id+"F20.imprint","IMPRINT",EDGE,{"derivedFrom":sQuery(id+"F20.wireOp",EDGE,"E67.0")}),1.0]])]});
            var Q1;
            Q1=makeQuery(id+"F20.imprint","IMPRINT",FACE,{"disambiguationData":[TD([[makeQuery(id+"F20.imprint","IMPRINT",EDGE,{"derivedFrom":sQuery(id+"F20.wireOp",EDGE,"E68.0")}),1.0]])]});
            extrude(context, id + "F22", {"entities" : qUnion([Q0, Q1]), "operationType" : NewBodyOperationType.REMOVE, "oppositeDirection" : true, "depth" : 3 * mm});
        }
        {
            var Q0;
            Q0=makeQuery(id+"F1.opExtrude","CAP_FACE",FACE,{"disambiguationData":[OSD([sQuery(id+"F0.wireOp",EDGE,"E0.top"),sQuery(id+"F0.wireOp",EDGE,"E0.left"),sQuery(id+"F0.wireOp",EDGE,"E0.right"),sQuery(id+"F0.wireOp",EDGE,"E1.1"),sQuery(id+"F0.wireOp",EDGE,"E2.filletArc"),sQuery(id+"F0.wireOp",EDGE,"E3.filletArc"),sQuery(id+"F0.wireOp",EDGE,"E4.filletArc"),sQuery(id+"F0.wireOp",EDGE,"E5.filletArc"),sQuery(id+"F0.wireOp",EDGE,"E6.filletArc"),sQuery(id+"F0.wireOp",EDGE,"E7.filletArc"),sQuery(id+"F0.wireOp",EDGE,"E8.filletArc"),sQuery(id+"F0.wireOp",EDGE,"E10"),sQuery(id+"F0.wireOp",EDGE,"E11"),sQuery(id+"F0.wireOp",EDGE,"E12"),sQuery(id+"F0.wireOp",EDGE,"E13.top"),sQuery(id+"F0.wireOp",EDGE,"E14"),sQuery(id+"F0.wireOp",EDGE,"E15"),sQuery(id+"F0.wireOp",EDGE,"E16"),sQuery(id+"F0.wireOp",EDGE,"E17"),sQuery(id+"F0.wireOp",EDGE,"E18"),sQuery(id+"F0.wireOp",EDGE,"E19"),sQuery(id+"F0.wireOp",EDGE,"E20.filletArc"),sQuery(id+"F0.wireOp",EDGE,"E21.filletArc"),sQuery(id+"F0.wireOp",EDGE,"E22.filletArc"),sQuery(id+"F0.wireOp",EDGE,"E23.filletArc"),sQuery(id+"F0.wireOp",EDGE,"E13.bottom"),sQuery(id+"F0.wireOp",EDGE,"E24.trimOffspring"),sQuery(id+"F0.wireOp",EDGE,"E25.filletArc"),sQuery(id+"F0.wireOp",EDGE,"E26.filletArc"),sQuery(id+"F0.wireOp",EDGE,"E27.filletArc"),sQuery(id+"F0.wireOp",EDGE,"E28"),sQuery(id+"F0.wireOp",EDGE,"E29"),sQuery(id+"F0.wireOp",EDGE,"E30.trimOffspring"),sQuery(id+"F0.wireOp",EDGE,"E32.filletArc"),sQuery(id+"F0.wireOp",EDGE,"E33.filletArc"),sQuery(id+"F0.wireOp",EDGE,"E34.filletArc"),sQuery(id+"F0.wireOp",EDGE,"E35.filletArc"),sQuery(id+"F0.wireOp",EDGE,"E39"),sQuery(id+"F0.wireOp",EDGE,"E40"),sQuery(id+"F0.wireOp",EDGE,"E41.trimOffspring"),sQuery(id+"F0.wireOp",EDGE,"E44.filletArc"),sQuery(id+"F0.wireOp",EDGE,"E45.filletArc"),sQuery(id+"F0.wireOp",EDGE,"E48"),sQuery(id+"F0.wireOp",EDGE,"E49"),sQuery(id+"F0.wireOp",EDGE,"E50.filletArc"),sQuery(id+"F0.wireOp",EDGE,"E51.filletArc")])],"isStart":true});
            var sketch = newSketch(context, id + "F23", { "sketchPlane" : qUnion([Q0])});
            skLineSegment(sketch, "E71.0", {"start": v(-10.9, 48.9) * mm, "end": v(-35.9, 48.9) * mm});
            skArc(sketch, "E71.1", {"start": v(-37.9, 46.9) * mm, "mid": v(-37.31, 48.31) * mm, "end": v(-35.9, 48.9) * mm});
            skLineSegment(sketch, "E71.2", {"start": v(-10.9, 46.9) * mm, "end": v(-35.9, 46.9) * mm});
            skLineSegment(sketch, "E71.3", {"start": v(-35.9, 46.9) * mm, "end": v(-35.9, -25.1) * mm});
            skLineSegment(sketch, "E71.4", {"start": v(-37.9, -25.1) * mm, "end": v(-37.9, 46.9) * mm});
            skArc(sketch, "E71.5", {"start": v(-31.9, 38.9) * mm, "mid": v(-30.73, 41.73) * mm, "end": v(-27.9, 42.9) * mm});
            skLineSegment(sketch, "E71.6", {"start": v(-27.9, 42.9) * mm, "end": v(-10.9, 42.9) * mm});
            skLineSegment(sketch, "E71.7", {"start": v(-27.9, 40.9) * mm, "end": v(-10.9, 40.9) * mm});
            skArc(sketch, "E71.8", {"start": v(-29.9, 38.9) * mm, "mid": v(-29.31, 40.31) * mm, "end": v(-27.9, 40.9) * mm});
            skLineSegment(sketch, "E71.9", {"start": v(-29.9, -17.1) * mm, "end": v(-29.9, 34.9) * mm});
            skLineSegment(sketch, "E71.10", {"start": v(-31.9, -17.1) * mm, "end": v(-31.9, 38.9) * mm});
            skArc(sketch, "E71.11", {"start": v(-8.9, 42.9) * mm, "mid": v(-9.49, 41.49) * mm, "end": v(-10.9, 40.9) * mm});
            skLineSegment(sketch, "E71.12", {"start": v(-10.9, 42.9) * mm, "end": v(-10.9, 46.9) * mm});
            skLineSegment(sketch, "E71.13", {"start": v(-8.9, 46.9) * mm, "end": v(-8.9, 42.9) * mm});
            skArc(sketch, "E71.14", {"start": v(-10.9, 48.9) * mm, "mid": v(-9.49, 48.31) * mm, "end": v(-8.9, 46.9) * mm});
            skArc(sketch, "E71.15", {"start": v(12.1, 46.9) * mm, "mid": v(12.69, 48.31) * mm, "end": v(14.1, 48.9) * mm});
            skLineSegment(sketch, "E71.16", {"start": v(36.1, 48.9) * mm, "end": v(14.1, 48.9) * mm});
            skLineSegment(sketch, "E71.17", {"start": v(36.1, 46.9) * mm, "end": v(14.1, 46.9) * mm});
            skLineSegment(sketch, "E71.18", {"start": v(14.1, 46.9) * mm, "end": v(14.1, 42.9) * mm});
            skLineSegment(sketch, "E71.19", {"start": v(14.1, 42.9) * mm, "end": v(28.1, 42.9) * mm});
            skArc(sketch, "E71.20", {"start": v(14.1, 40.9) * mm, "mid": v(12.69, 41.49) * mm, "end": v(12.1, 42.9) * mm});
            skLineSegment(sketch, "E71.21", {"start": v(14.1, 40.9) * mm, "end": v(28.1, 40.9) * mm});
            skLineSegment(sketch, "E71.22", {"start": v(12.1, 46.9) * mm, "end": v(12.1, 42.9) * mm});
            skArc(sketch, "E71.23", {"start": v(36.1, 48.9) * mm, "mid": v(37.51, 48.31) * mm, "end": v(38.1, 46.9) * mm});
            skLineSegment(sketch, "E71.24", {"start": v(38.1, 46.9) * mm, "end": v(38.1, -25.1) * mm});
            skLineSegment(sketch, "E71.25", {"start": v(36.1, -25.1) * mm, "end": v(36.1, 46.9) * mm});
            skArc(sketch, "E71.26", {"start": v(28.1, 42.9) * mm, "mid": v(30.93, 41.73) * mm, "end": v(32.1, 38.9) * mm});
            skLineSegment(sketch, "E71.27", {"start": v(32.1, 38.9) * mm, "end": v(32.1, -17.1) * mm});
            skArc(sketch, "E71.28", {"start": v(28.1, 40.9) * mm, "mid": v(29.51, 40.31) * mm, "end": v(30.1, 38.9) * mm});
            skLineSegment(sketch, "E71.29", {"start": v(30.1, -17.1) * mm, "end": v(30.1, 38.9) * mm});
            skLineSegment(sketch, "E71.30", {"start": v(28.1, -19.1) * mm, "end": v(-27.9, -19.1) * mm});
            skArc(sketch, "E71.31", {"start": v(32.1, -17.1) * mm, "mid": v(30.93, -19.93) * mm, "end": v(28.1, -21.1) * mm});
            skArc(sketch, "E71.32", {"start": v(30.1, -17.1) * mm, "mid": v(29.51, -18.51) * mm, "end": v(28.1, -19.1) * mm});
            skLineSegment(sketch, "E71.33", {"start": v(28.1, -21.1) * mm, "end": v(-27.9, -21.1) * mm});
            skArc(sketch, "E71.34", {"start": v(-27.9, -21.1) * mm, "mid": v(-30.73, -19.93) * mm, "end": v(-31.9, -17.1) * mm});
            skArc(sketch, "E71.35", {"start": v(-27.9, -19.1) * mm, "mid": v(-29.31, -18.51) * mm, "end": v(-29.9, -17.1) * mm});
            skLineSegment(sketch, "E71.36", {"start": v(-35.9, -25.1) * mm, "end": v(-29.9, -25.1) * mm});
            skArc(sketch, "E71.37", {"start": v(-35.9, -27.1) * mm, "mid": v(-37.31, -26.51) * mm, "end": v(-37.9, -25.1) * mm});
            skLineSegment(sketch, "E71.38", {"start": v(-29.9, -27.1) * mm, "end": v(-35.9, -27.1) * mm});
            skArc(sketch, "E71.39", {"start": v(-29.9, -27.1) * mm, "mid": v(-28.49, -27.69) * mm, "end": v(-27.9, -29.1) * mm});
            skArc(sketch, "E71.40", {"start": v(-29.9, -25.1) * mm, "mid": v(-27.07, -26.27) * mm, "end": v(-25.9, -29.1) * mm});
            skLineSegment(sketch, "E71.41", {"start": v(-22.9, -40.37) * mm, "end": v(-22.9, -25.1) * mm});
            skLineSegment(sketch, "E71.42", {"start": v(-22.9, -25.1) * mm, "end": v(23.1, -25.1) * mm});
            skLineSegment(sketch, "E71.43", {"start": v(-20.9, -27.1) * mm, "end": v(-20.9, -40.37) * mm});
            skLineSegment(sketch, "E71.44", {"start": v(21.1, -27.1) * mm, "end": v(-20.9, -27.1) * mm});
            skLineSegment(sketch, "E71.45", {"start": v(-25.9, -29.1) * mm, "end": v(-25.9, -47.37) * mm});
            skLineSegment(sketch, "E71.46", {"start": v(-27.9, -45.37) * mm, "end": v(-27.9, -31.1) * mm});
            skLineSegment(sketch, "E71.47", {"start": v(-27.9, -47.37) * mm, "end": v(-27.9, -29.1) * mm});
            skArc(sketch, "E71.48", {"start": v(-18.9, -44.37) * mm, "mid": v(-21.73, -43.2) * mm, "end": v(-22.9, -40.37) * mm});
            skArc(sketch, "E71.49", {"start": v(-18.9, -42.37) * mm, "mid": v(-20.31, -41.78) * mm, "end": v(-20.9, -40.37) * mm});
            skLineSegment(sketch, "E71.50", {"start": v(-4, -42.37) * mm, "end": v(-18.9, -42.37) * mm});
            skLineSegment(sketch, "E71.51", {"start": v(-4, -44.37) * mm, "end": v(-18.9, -44.37) * mm});
            skLineSegment(sketch, "E71.52", {"start": v(-25.9, -47.37) * mm, "end": v(-4, -47.37) * mm});
            skArc(sketch, "E71.53", {"start": v(-25.9, -49.37) * mm, "mid": v(-27.31, -48.78) * mm, "end": v(-27.9, -47.37) * mm});
            skLineSegment(sketch, "E71.54", {"start": v(-6, -49.37) * mm, "end": v(-23.9, -49.37) * mm});
            skLineSegment(sketch, "E71.55", {"start": v(-4, -49.37) * mm, "end": v(-25.9, -49.37) * mm});
            skArc(sketch, "E71.56", {"start": v(-2, -47.37) * mm, "mid": v(-2.59, -48.78) * mm, "end": v(-4, -49.37) * mm});
            skLineSegment(sketch, "E71.57", {"start": v(-4, -47.37) * mm, "end": v(-4, -44.37) * mm});
            skLineSegment(sketch, "E71.58", {"start": v(-2, -44.37) * mm, "end": v(-2, -47.37) * mm});
            skArc(sketch, "E71.59", {"start": v(-4, -42.37) * mm, "mid": v(-2.59, -42.95) * mm, "end": v(-2, -44.37) * mm});
            skArc(sketch, "E71.60", {"start": v(2, -44.37) * mm, "mid": v(2.59, -42.95) * mm, "end": v(4, -42.37) * mm});
            skLineSegment(sketch, "E71.61", {"start": v(2, -44.37) * mm, "end": v(2, -47.37) * mm});
            skArc(sketch, "E71.62", {"start": v(4, -49.37) * mm, "mid": v(2.59, -48.78) * mm, "end": v(2, -47.37) * mm});
            skLineSegment(sketch, "E71.63", {"start": v(26.1, -49.37) * mm, "end": v(4, -49.37) * mm});
            skLineSegment(sketch, "E71.64", {"start": v(4, -47.37) * mm, "end": v(26.1, -47.37) * mm});
            skLineSegment(sketch, "E71.65", {"start": v(4, -44.37) * mm, "end": v(4, -47.37) * mm});
            skLineSegment(sketch, "E71.66", {"start": v(19.1, -44.37) * mm, "end": v(4, -44.37) * mm});
            skArc(sketch, "E71.67", {"start": v(23.1, -40.37) * mm, "mid": v(21.93, -43.2) * mm, "end": v(19.1, -44.37) * mm});
            skLineSegment(sketch, "E71.68", {"start": v(26.1, -47.37) * mm, "end": v(26.1, -29.1) * mm});
            skArc(sketch, "E71.69", {"start": v(28.1, -47.37) * mm, "mid": v(27.51, -48.78) * mm, "end": v(26.1, -49.37) * mm});
            skLineSegment(sketch, "E71.70", {"start": v(28.1, -31.1) * mm, "end": v(28.1, -45.37) * mm});
            skLineSegment(sketch, "E71.71", {"start": v(28.1, -29.1) * mm, "end": v(28.1, -47.37) * mm});
            skLineSegment(sketch, "E71.72", {"start": v(23.1, -25.1) * mm, "end": v(23.1, -40.37) * mm});
            skLineSegment(sketch, "E71.73", {"start": v(21.1, -27.1) * mm, "end": v(21.1, -40.37) * mm});
            skLineSegment(sketch, "E71.74", {"start": v(19.1, -42.37) * mm, "end": v(4, -42.37) * mm});
            skArc(sketch, "E71.75", {"start": v(21.1, -40.37) * mm, "mid": v(20.51, -41.78) * mm, "end": v(19.1, -42.37) * mm});
            skArc(sketch, "E71.76", {"start": v(26.1, -29.1) * mm, "mid": v(27.27, -26.27) * mm, "end": v(30.1, -25.1) * mm});
            skArc(sketch, "E71.77", {"start": v(28.1, -29.1) * mm, "mid": v(28.69, -27.69) * mm, "end": v(30.1, -27.1) * mm});
            skLineSegment(sketch, "E71.78", {"start": v(36.1, -27.1) * mm, "end": v(30.1, -27.1) * mm});
            skLineSegment(sketch, "E71.79", {"start": v(30.1, -25.1) * mm, "end": v(36.1, -25.1) * mm});
            skArc(sketch, "E71.80", {"start": v(38.1, -25.1) * mm, "mid": v(37.51, -26.51) * mm, "end": v(36.1, -27.1) * mm});
            skLineSegment(sketch, "E72", {"start": v(-29.9, -27.1) * mm, "end": v(-29.9, -17.1) * mm});
            skLineSegment(sketch, "E73", {"start": v(-29.9, -17.1) * mm, "end": v(-29.9, -15.1) * mm});
            skLineSegment(sketch, "E74", {"start": v(-29.9, 10.9) * mm, "end": v(-29.9, 34.9) * mm});
            skLineSegment(sketch, "E75", {"start": v(-29.9, 10.9) * mm, "end": v(-29.9, -13.1) * mm});
            skPoint(sketch, "E76.orphan", {"position": v(-37.9, 34.9) * mm});
            skLineSegment(sketch, "E77", {"start": v(-29.9, -13.1) * mm, "end": v(-29.9, -10.1) * mm});
            skLineSegment(sketch, "E78", {"start": v(-29.89, -7.76) * mm, "end": v(-29.9, -6.76) * mm});
            skPoint(sketch, "E79.end.orphan", {"position": v(-29.9, 36.9) * mm});
            skLineSegment(sketch, "E80.trimOffspring", {"start": v(-29.9, 46.9) * mm, "end": v(-29.9, 48.9) * mm});
            skLineSegment(sketch, "E81", {"start": v(-29.9, 46.9) * mm, "end": v(-29.9, 29.9) * mm});
            skLineSegment(sketch, "E82", {"start": v(-29.9, 29.9) * mm, "end": v(-29.9, 30.9) * mm});
            skLineSegment(sketch, "E83", {"start": v(-29.9, 30.9) * mm, "end": v(-29.9, 31.9) * mm});
            skLineSegment(sketch, "E84", {"start": v(-29.84, 31.9) * mm, "end": v(-37.9, 31.9) * mm});
            skPoint(sketch, "E85.end.orphan", {"position": v(-29.89, -7.76) * mm});
            skPoint(sketch, "E86.orphan", {"position": v(-29.87, -8.76) * mm});
            skLineSegment(sketch, "E87", {"start": v(-29.9, -17.1) * mm, "end": v(-29.9, -10.1) * mm});
            skLineSegment(sketch, "E88", {"start": v(-29.9, -10.1) * mm, "end": v(-37.9, -10.1) * mm});
            skLineSegment(sketch, "E89", {"start": v(-29.9, 40.9) * mm, "end": v(-37.9, 40.9) * mm});
            skPoint(sketch, "E90.end.orphan", {"position": v(-37.9, 38.9) * mm});
            skLineSegment(sketch, "E91", {"start": v(-29.9, -19.1) * mm, "end": v(-37.9, -19.1) * mm});
            skCircle(sketch, "E92", {"center": v(-33.9, 36.9) * mm, "radius": 1.5 * mm});
            skPoint(sketch, "E92.centerSnap0", {"position": v(-33.9, 40.9) * mm});
            skCircle(sketch, "E93", {"center": v(-33.9, -14.39) * mm, "radius": 1.5 * mm});
            skPoint(sketch, "E93.centerSnap0", {"position": v(-33.9, -10.1) * mm});
            skSolve(sketch);
        }
        {
            var Q0;
            {var subQ0=sQuery(id+"F23.wireOp",EDGE,"E89");var subQ1=sQuery(id+"F23.wireOp",EDGE,"E71.3");var subQ2=makeQuery(id+"F23.imprint","INTERSECT",VERTEX,{"derivedFrom":[subQ1,subQ0]});Q0=makeQuery(id+"F23.imprint","IMPRINT",FACE,{"disambiguationData":[TD([[makeQuery(id+"F23.imprint","IMPRINT",EDGE,{"disambiguationData":[TD([[subQ2,-1.0]])],"derivedFrom":subQ1}),-1.0]])]});}
            var Q1;
            {var subQ0=sQuery(id+"F23.wireOp",EDGE,"E88");var subQ1=sQuery(id+"F23.wireOp",EDGE,"E71.3");var subQ2=makeQuery(id+"F23.imprint","INTERSECT",VERTEX,{"derivedFrom":[subQ1,subQ0]});Q1=makeQuery(id+"F23.imprint","IMPRINT",FACE,{"disambiguationData":[TD([[makeQuery(id+"F23.imprint","IMPRINT",EDGE,{"disambiguationData":[TD([[subQ2,-1.0]])],"derivedFrom":subQ1}),-1.0]])]});}
            var Q2;
            {var subQ6=sQuery(id+"F23.wireOp",EDGE,"E71.10");var subQ7=sQuery(id+"F23.wireOp",EDGE,"E71.5");var subQ8=makeQuery(id+"F23.imprint","INTERSECT",VERTEX,{"derivedFrom":[subQ7,subQ6]});Q2=makeQuery(id+"F23.imprint","IMPRINT",FACE,{"disambiguationData":[TD([[makeQuery(id+"F23.imprint","IMPRINT",EDGE,{"disambiguationData":[TD([[subQ8,-1.0]])],"derivedFrom":subQ7}),-1.0]])]});}
            var Q3;
            {var subQ3=sQuery(id+"F23.wireOp",EDGE,"E88");var subQ7=sQuery(id+"F23.wireOp",EDGE,"E71.3");var subQ8=makeQuery(id+"F23.imprint","INTERSECT",VERTEX,{"derivedFrom":[subQ7,subQ3]});Q3=makeQuery(id+"F23.imprint","IMPRINT",FACE,{"disambiguationData":[TD([[makeQuery(id+"F23.imprint","IMPRINT",EDGE,{"disambiguationData":[TD([[subQ8,-1.0]])],"derivedFrom":subQ7}),1.0]])]});}
            var Q4;
            {var subQ0=sQuery(id+"F23.wireOp",EDGE,"E88");var subQ1=sQuery(id+"F23.wireOp",EDGE,"E71.3");var subQ2=makeQuery(id+"F23.imprint","INTERSECT",VERTEX,{"derivedFrom":[subQ1,subQ0]});Q4=makeQuery(id+"F23.imprint","IMPRINT",FACE,{"disambiguationData":[TD([[makeQuery(id+"F23.imprint","IMPRINT",EDGE,{"disambiguationData":[TD([[subQ2,-1.0]])],"derivedFrom":subQ1}),-1.0]])]});}
            var Q5;
            {var subQ5=sQuery(id+"F23.wireOp",EDGE,"E71.34");var subQ7=sQuery(id+"F23.wireOp",EDGE,"E71.10");var subQ8=makeQuery(id+"F23.imprint","INTERSECT",VERTEX,{"derivedFrom":[subQ7,subQ5]});Q5=makeQuery(id+"F23.imprint","IMPRINT",FACE,{"disambiguationData":[TD([[makeQuery(id+"F23.imprint","IMPRINT",EDGE,{"disambiguationData":[TD([[subQ8,-1.0]])],"derivedFrom":subQ7}),-1.0]])]});}
            var Q6;
            {var subQ1=sQuery(id+"F23.wireOp",EDGE,"E71.3");var subQ7=sQuery(id+"F23.wireOp",EDGE,"E89");var subQ9=makeQuery(id+"F23.imprint","INTERSECT",VERTEX,{"derivedFrom":[subQ1,subQ7]});Q6=makeQuery(id+"F23.imprint","IMPRINT",FACE,{"disambiguationData":[TD([[makeQuery(id+"F23.imprint","IMPRINT",EDGE,{"disambiguationData":[TD([[subQ9,-1.0]])],"derivedFrom":subQ1}),1.0]])]});}
            var Q7;
            Q7=makeQuery(id+"F23.imprint","IMPRINT",FACE,{"disambiguationData":[TD([[makeQuery(id+"F23.imprint","IMPRINT",EDGE,{"derivedFrom":sQuery(id+"F23.wireOp",EDGE,"E92")}),1.0]])]});
            var Q8;
            Q8=makeQuery(id+"F23.imprint","IMPRINT",FACE,{"disambiguationData":[TD([[makeQuery(id+"F23.imprint","IMPRINT",EDGE,{"derivedFrom":sQuery(id+"F23.wireOp",EDGE,"E93")}),1.0]])]});
            extrude(context, id + "F24", {"entities" : qUnion([Q0, Q1, Q2, Q3, Q4, Q5, Q6, Q7, Q8]), "operationType" : NewBodyOperationType.ADD, "depth" : 56 * mm});
        }
        {
            var Q0;
            {var subQ0=sQuery(id+"F23.wireOp",EDGE,"E71.4");Q0=makeQuery(id+"FEf3B15wsktiEYm_1.boolean.opBoolean","MERGE",FACE,{"derivedFrom":[makeQuery(id+"F24.boolean.opBoolean","MERGE",FACE,{"derivedFrom":[makeQuery(id+"F1.opExtrude","SWEPT_FACE",FACE,{"disambiguationData":[OSD([sQuery(id+"F0.wireOp",EDGE,"E1.1")])]}),makeQuery(id+"F24.opExtrude","SWEPT_FACE",FACE,{"disambiguationData":[OSD([subQ0]),TDD([makeQuery(id+"F23.imprint","IMPRINT",EDGE,{"disambiguationData":[TD([[makeQuery(id+"F23.imprint","INTERSECT",VERTEX,{"derivedFrom":[subQ0,sQuery(id+"F23.wireOp",EDGE,"E71.37")]}),-1.0]])],"derivedFrom":subQ0})])]}),makeQuery(id+"F24.opExtrude","SWEPT_FACE",FACE,{"disambiguationData":[OSD([subQ0]),TDD([makeQuery(id+"F23.imprint","IMPRINT",EDGE,{"disambiguationData":[TD([[makeQuery(id+"F23.imprint","INTERSECT",VERTEX,{"derivedFrom":[sQuery(id+"F23.wireOp",EDGE,"E71.1"),subQ0]}),1.0]])],"derivedFrom":subQ0})])]})]}),makeQuery(id+"FEf3B15wsktiEYm_1.opExtrude","SWEPT_FACE",FACE,{"disambiguationData":[OSD([sQuery(id+"F0yRP5bMj2yEoty_1.wireOp",EDGE,"abbe0a9e-e51f-4a6a-ba4b-c54c44bda86f.4")])]})]});}
            var sketch = newSketch(context, id + "F25", { "sketchPlane" : qUnion([Q0])});
            skLineSegment(sketch, "E94", {"start": v(2.7, 36.17) * mm, "end": v(53.4, 36.17) * mm});
            skLineSegment(sketch, "E95", {"start": v(53.4, 36.17) * mm, "end": v(53.4, -14.53) * mm});
            skLineSegment(sketch, "E96", {"start": v(53.4, -14.53) * mm, "end": v(2.7, -14.53) * mm});
            skLineSegment(sketch, "E97", {"start": v(2.7, -14.53) * mm, "end": v(2.7, 36.17) * mm});
            skLineSegment(sketch, "E98", {"start": v(-0.84, 39.74) * mm, "end": v(56.76, 39.74) * mm});
            skLineSegment(sketch, "E99", {"start": v(56.76, 39.74) * mm, "end": v(56.76, -17.86) * mm});
            skLineSegment(sketch, "E100", {"start": v(56.76, -17.86) * mm, "end": v(-0.84, -17.86) * mm});
            skLineSegment(sketch, "E101", {"start": v(-0.84, -17.86) * mm, "end": v(-0.84, 39.74) * mm});
            skCircle(sketch, "E102", {"center": v(2.7, 36.17) * mm, "radius": 1 * mm});
            skCircle(sketch, "E103", {"center": v(53.4, 36.17) * mm, "radius": 1 * mm});
            skCircle(sketch, "E104", {"center": v(2.7, -14.53) * mm, "radius": 1 * mm});
            skCircle(sketch, "E105", {"center": v(53.4, -14.53) * mm, "radius": 1 * mm});
            skSolve(sketch);
        }
        {
            var Q0;
            Q0=makeQuery(id+"F24.opExtrude","CAP_FACE",FACE,{"disambiguationData":[OSD([sQuery(id+"F23.wireOp",EDGE,"E71.4"),sQuery(id+"F23.wireOp",EDGE,"E81"),sQuery(id+"F23.wireOp",EDGE,"E83"),sQuery(id+"F23.wireOp",EDGE,"E84"),sQuery(id+"F23.wireOp",EDGE,"E89")])],"isStart":false});
            var sketch = newSketch(context, id + "F26", { "sketchPlane" : qUnion([Q0])});
            skLineSegment(sketch, "E106.0", {"start": v(-10.9, 48.9) * mm, "end": v(-35.9, 48.9) * mm});
            skArc(sketch, "E106.1", {"start": v(-37.9, 46.9) * mm, "mid": v(-37.31, 48.31) * mm, "end": v(-35.9, 48.9) * mm});
            skLineSegment(sketch, "E106.2", {"start": v(-10.9, 46.9) * mm, "end": v(-35.9, 46.9) * mm});
            skLineSegment(sketch, "E106.3", {"start": v(-35.9, 46.9) * mm, "end": v(-35.9, -25.1) * mm});
            skLineSegment(sketch, "E106.4", {"start": v(-37.9, -25.1) * mm, "end": v(-37.9, 46.9) * mm});
            skArc(sketch, "E106.5", {"start": v(-31.9, 38.9) * mm, "mid": v(-30.73, 41.73) * mm, "end": v(-27.9, 42.9) * mm});
            skLineSegment(sketch, "E106.6", {"start": v(-27.9, 42.9) * mm, "end": v(-10.9, 42.9) * mm});
            skLineSegment(sketch, "E106.7", {"start": v(-27.9, 40.9) * mm, "end": v(-10.9, 40.9) * mm});
            skArc(sketch, "E106.8", {"start": v(-29.9, 38.9) * mm, "mid": v(-29.31, 40.31) * mm, "end": v(-27.9, 40.9) * mm});
            skLineSegment(sketch, "E106.9", {"start": v(-29.9, -17.1) * mm, "end": v(-29.9, 34.9) * mm});
            skLineSegment(sketch, "E106.10", {"start": v(-31.9, -17.1) * mm, "end": v(-31.9, 38.9) * mm});
            skArc(sketch, "E106.11", {"start": v(-8.9, 42.9) * mm, "mid": v(-9.49, 41.49) * mm, "end": v(-10.9, 40.9) * mm});
            skLineSegment(sketch, "E106.12", {"start": v(-10.9, 42.9) * mm, "end": v(-10.9, 46.9) * mm});
            skLineSegment(sketch, "E106.13", {"start": v(-8.9, 46.9) * mm, "end": v(-8.9, 42.9) * mm});
            skArc(sketch, "E106.14", {"start": v(-10.9, 48.9) * mm, "mid": v(-9.49, 48.31) * mm, "end": v(-8.9, 46.9) * mm});
            skArc(sketch, "E106.15", {"start": v(12.1, 46.9) * mm, "mid": v(12.69, 48.31) * mm, "end": v(14.1, 48.9) * mm});
            skLineSegment(sketch, "E106.16", {"start": v(36.1, 48.9) * mm, "end": v(14.1, 48.9) * mm});
            skLineSegment(sketch, "E106.17", {"start": v(36.1, 46.9) * mm, "end": v(14.1, 46.9) * mm});
            skLineSegment(sketch, "E106.18", {"start": v(14.1, 46.9) * mm, "end": v(14.1, 42.9) * mm});
            skLineSegment(sketch, "E106.19", {"start": v(14.1, 42.9) * mm, "end": v(28.1, 42.9) * mm});
            skArc(sketch, "E106.20", {"start": v(14.1, 40.9) * mm, "mid": v(12.69, 41.49) * mm, "end": v(12.1, 42.9) * mm});
            skLineSegment(sketch, "E106.21", {"start": v(14.1, 40.9) * mm, "end": v(28.1, 40.9) * mm});
            skLineSegment(sketch, "E106.22", {"start": v(12.1, 46.9) * mm, "end": v(12.1, 42.9) * mm});
            skArc(sketch, "E106.23", {"start": v(36.1, 48.9) * mm, "mid": v(37.51, 48.31) * mm, "end": v(38.1, 46.9) * mm});
            skLineSegment(sketch, "E106.24", {"start": v(38.1, 46.9) * mm, "end": v(38.1, -25.1) * mm});
            skLineSegment(sketch, "E106.25", {"start": v(36.1, -25.1) * mm, "end": v(36.1, 46.9) * mm});
            skArc(sketch, "E106.26", {"start": v(28.1, 42.9) * mm, "mid": v(30.93, 41.73) * mm, "end": v(32.1, 38.9) * mm});
            skLineSegment(sketch, "E106.27", {"start": v(32.1, 38.9) * mm, "end": v(32.1, -17.1) * mm});
            skArc(sketch, "E106.28", {"start": v(28.1, 40.9) * mm, "mid": v(29.51, 40.31) * mm, "end": v(30.1, 38.9) * mm});
            skLineSegment(sketch, "E106.29", {"start": v(30.1, -17.1) * mm, "end": v(30.1, 38.9) * mm});
            skLineSegment(sketch, "E106.30", {"start": v(28.1, -19.1) * mm, "end": v(-27.9, -19.1) * mm});
            skArc(sketch, "E106.31", {"start": v(32.1, -17.1) * mm, "mid": v(30.93, -19.93) * mm, "end": v(28.1, -21.1) * mm});
            skArc(sketch, "E106.32", {"start": v(30.1, -17.1) * mm, "mid": v(29.51, -18.51) * mm, "end": v(28.1, -19.1) * mm});
            skLineSegment(sketch, "E106.33", {"start": v(28.1, -21.1) * mm, "end": v(-27.9, -21.1) * mm});
            skArc(sketch, "E106.34", {"start": v(-27.9, -21.1) * mm, "mid": v(-30.73, -19.93) * mm, "end": v(-31.9, -17.1) * mm});
            skArc(sketch, "E106.35", {"start": v(-27.9, -19.1) * mm, "mid": v(-29.31, -18.51) * mm, "end": v(-29.9, -17.1) * mm});
            skLineSegment(sketch, "E106.36", {"start": v(-35.9, -25.1) * mm, "end": v(-29.9, -25.1) * mm});
            skArc(sketch, "E106.37", {"start": v(-35.9, -27.1) * mm, "mid": v(-37.31, -26.51) * mm, "end": v(-37.9, -25.1) * mm});
            skLineSegment(sketch, "E106.38", {"start": v(-29.9, -27.1) * mm, "end": v(-35.9, -27.1) * mm});
            skArc(sketch, "E106.39", {"start": v(-29.9, -27.1) * mm, "mid": v(-28.49, -27.69) * mm, "end": v(-27.9, -29.1) * mm});
            skArc(sketch, "E106.40", {"start": v(-29.9, -25.1) * mm, "mid": v(-27.07, -26.27) * mm, "end": v(-25.9, -29.1) * mm});
            skLineSegment(sketch, "E106.41", {"start": v(-22.9, -40.37) * mm, "end": v(-22.9, -25.1) * mm});
            skLineSegment(sketch, "E106.42", {"start": v(-22.9, -25.1) * mm, "end": v(23.1, -25.1) * mm});
            skLineSegment(sketch, "E106.43", {"start": v(-20.9, -27.1) * mm, "end": v(-20.9, -40.37) * mm});
            skLineSegment(sketch, "E106.44", {"start": v(21.1, -27.1) * mm, "end": v(-20.9, -27.1) * mm});
            skLineSegment(sketch, "E106.45", {"start": v(-25.9, -29.1) * mm, "end": v(-25.9, -47.37) * mm});
            skLineSegment(sketch, "E106.46", {"start": v(-27.9, -45.37) * mm, "end": v(-27.9, -31.1) * mm});
            skLineSegment(sketch, "E106.47", {"start": v(-27.9, -47.37) * mm, "end": v(-27.9, -29.1) * mm});
            skArc(sketch, "E106.48", {"start": v(-18.9, -44.37) * mm, "mid": v(-21.73, -43.2) * mm, "end": v(-22.9, -40.37) * mm});
            skArc(sketch, "E106.49", {"start": v(-18.9, -42.37) * mm, "mid": v(-20.31, -41.78) * mm, "end": v(-20.9, -40.37) * mm});
            skLineSegment(sketch, "E106.50", {"start": v(-4, -42.37) * mm, "end": v(-18.9, -42.37) * mm});
            skLineSegment(sketch, "E106.51", {"start": v(-4, -44.37) * mm, "end": v(-18.9, -44.37) * mm});
            skLineSegment(sketch, "E106.52", {"start": v(-25.9, -47.37) * mm, "end": v(-4, -47.37) * mm});
            skArc(sketch, "E106.53", {"start": v(-25.9, -49.37) * mm, "mid": v(-27.31, -48.78) * mm, "end": v(-27.9, -47.37) * mm});
            skLineSegment(sketch, "E106.54", {"start": v(-6, -49.37) * mm, "end": v(-23.9, -49.37) * mm});
            skLineSegment(sketch, "E106.55", {"start": v(-4, -49.37) * mm, "end": v(-25.9, -49.37) * mm});
            skArc(sketch, "E106.56", {"start": v(-2, -47.37) * mm, "mid": v(-2.59, -48.78) * mm, "end": v(-4, -49.37) * mm});
            skLineSegment(sketch, "E106.57", {"start": v(-4, -47.37) * mm, "end": v(-4, -44.37) * mm});
            skLineSegment(sketch, "E106.58", {"start": v(-2, -44.37) * mm, "end": v(-2, -47.37) * mm});
            skArc(sketch, "E106.59", {"start": v(-4, -42.37) * mm, "mid": v(-2.59, -42.95) * mm, "end": v(-2, -44.37) * mm});
            skArc(sketch, "E106.60", {"start": v(2, -44.37) * mm, "mid": v(2.59, -42.95) * mm, "end": v(4, -42.37) * mm});
            skLineSegment(sketch, "E106.61", {"start": v(2, -44.37) * mm, "end": v(2, -47.37) * mm});
            skArc(sketch, "E106.62", {"start": v(4, -49.37) * mm, "mid": v(2.59, -48.78) * mm, "end": v(2, -47.37) * mm});
            skLineSegment(sketch, "E106.63", {"start": v(26.1, -49.37) * mm, "end": v(4, -49.37) * mm});
            skLineSegment(sketch, "E106.64", {"start": v(4, -47.37) * mm, "end": v(26.1, -47.37) * mm});
            skLineSegment(sketch, "E106.65", {"start": v(4, -44.37) * mm, "end": v(4, -47.37) * mm});
            skLineSegment(sketch, "E106.66", {"start": v(19.1, -44.37) * mm, "end": v(4, -44.37) * mm});
            skArc(sketch, "E106.67", {"start": v(23.1, -40.37) * mm, "mid": v(21.93, -43.2) * mm, "end": v(19.1, -44.37) * mm});
            skLineSegment(sketch, "E106.68", {"start": v(26.1, -47.37) * mm, "end": v(26.1, -29.1) * mm});
            skArc(sketch, "E106.69", {"start": v(28.1, -47.37) * mm, "mid": v(27.51, -48.78) * mm, "end": v(26.1, -49.37) * mm});
            skLineSegment(sketch, "E106.70", {"start": v(28.1, -31.1) * mm, "end": v(28.1, -45.37) * mm});
            skLineSegment(sketch, "E106.71", {"start": v(28.1, -29.1) * mm, "end": v(28.1, -47.37) * mm});
            skLineSegment(sketch, "E106.72", {"start": v(23.1, -25.1) * mm, "end": v(23.1, -40.37) * mm});
            skLineSegment(sketch, "E106.73", {"start": v(21.1, -27.1) * mm, "end": v(21.1, -40.37) * mm});
            skLineSegment(sketch, "E106.74", {"start": v(19.1, -42.37) * mm, "end": v(4, -42.37) * mm});
            skArc(sketch, "E106.75", {"start": v(21.1, -40.37) * mm, "mid": v(20.51, -41.78) * mm, "end": v(19.1, -42.37) * mm});
            skArc(sketch, "E106.76", {"start": v(26.1, -29.1) * mm, "mid": v(27.27, -26.27) * mm, "end": v(30.1, -25.1) * mm});
            skArc(sketch, "E106.77", {"start": v(28.1, -29.1) * mm, "mid": v(28.69, -27.69) * mm, "end": v(30.1, -27.1) * mm});
            skLineSegment(sketch, "E106.78", {"start": v(36.1, -27.1) * mm, "end": v(30.1, -27.1) * mm});
            skLineSegment(sketch, "E106.79", {"start": v(30.1, -25.1) * mm, "end": v(36.1, -25.1) * mm});
            skArc(sketch, "E106.80", {"start": v(38.1, -25.1) * mm, "mid": v(37.51, -26.51) * mm, "end": v(36.1, -27.1) * mm});
            skLineSegment(sketch, "E106.81", {"start": v(-29.9, -27.1) * mm, "end": v(-29.9, -17.1) * mm});
            skLineSegment(sketch, "E106.82", {"start": v(-29.9, -17.1) * mm, "end": v(-29.9, -15.1) * mm});
            skLineSegment(sketch, "E106.83", {"start": v(-29.9, 10.9) * mm, "end": v(-29.9, 34.9) * mm});
            skLineSegment(sketch, "E106.84", {"start": v(-29.9, 10.9) * mm, "end": v(-29.9, -13.1) * mm});
            skPoint(sketch, "E106.85", {"position": v(-37.9, 34.9) * mm});
            skLineSegment(sketch, "E106.86", {"start": v(-29.9, -13.1) * mm, "end": v(-29.9, -10.1) * mm});
            skLineSegment(sketch, "E106.87", {"start": v(-29.89, -7.76) * mm, "end": v(-29.9, -6.76) * mm});
            skPoint(sketch, "E106.88", {"position": v(-29.9, 36.9) * mm});
            skLineSegment(sketch, "E106.89", {"start": v(-29.9, 46.9) * mm, "end": v(-29.9, 48.9) * mm});
            skLineSegment(sketch, "E106.90", {"start": v(-29.9, 46.9) * mm, "end": v(-29.9, 29.9) * mm});
            skLineSegment(sketch, "E106.91", {"start": v(-29.9, 29.9) * mm, "end": v(-29.9, 30.9) * mm});
            skLineSegment(sketch, "E106.92", {"start": v(-29.9, 30.9) * mm, "end": v(-29.9, 31.9) * mm});
            skLineSegment(sketch, "E106.93", {"start": v(-29.84, 31.9) * mm, "end": v(-37.9, 31.9) * mm});
            skPoint(sketch, "E106.94", {"position": v(-29.89, -7.76) * mm});
            skPoint(sketch, "E106.95", {"position": v(-29.87, -8.76) * mm});
            skLineSegment(sketch, "E106.96", {"start": v(-29.9, -17.1) * mm, "end": v(-29.9, -10.1) * mm});
            skLineSegment(sketch, "E106.97", {"start": v(-29.9, -10.1) * mm, "end": v(-37.9, -10.1) * mm});
            skLineSegment(sketch, "E106.98", {"start": v(-29.9, 40.9) * mm, "end": v(-37.9, 40.9) * mm});
            skPoint(sketch, "E106.99", {"position": v(-37.9, 38.9) * mm});
            skLineSegment(sketch, "E106.100", {"start": v(-29.9, -19.1) * mm, "end": v(-37.9, -19.1) * mm});
            skLineSegment(sketch, "E107", {"start": v(-33.87, 31.9) * mm, "end": v(-33.87, -10.1) * mm});
            skLineSegment(sketch, "E108", {"start": v(-33.87, 31.9) * mm, "end": v(-34.86, 31.9) * mm});
            skLineSegment(sketch, "E109", {"start": v(-34.86, 31.9) * mm, "end": v(-34.86, -10.1) * mm});
            skSolve(sketch);
        }
        {
            var Q0;
            {var subQ1=sQuery(id+"F26.wireOp",EDGE,"E106.3");var subQ7=sQuery(id+"F26.wireOp",EDGE,"E106.98");var subQ8=makeQuery(id+"F26.imprint","INTERSECT",VERTEX,{"derivedFrom":[subQ1,subQ7]});Q0=makeQuery(id+"F26.imprint","IMPRINT",FACE,{"disambiguationData":[TD([[makeQuery(id+"F26.imprint","IMPRINT",EDGE,{"disambiguationData":[TD([[subQ8,-1.0]])],"derivedFrom":subQ1}),1.0]])]});}
            var Q1;
            {var subQ6=sQuery(id+"F26.wireOp",EDGE,"E106.10");var subQ7=sQuery(id+"F26.wireOp",EDGE,"E106.5");var subQ8=makeQuery(id+"F26.imprint","INTERSECT",VERTEX,{"derivedFrom":[subQ7,subQ6]});Q1=makeQuery(id+"F26.imprint","IMPRINT",FACE,{"disambiguationData":[TD([[makeQuery(id+"F26.imprint","IMPRINT",EDGE,{"disambiguationData":[TD([[subQ8,-1.0]])],"derivedFrom":subQ7}),-1.0]])]});}
            var Q2;
            {var subQ0=sQuery(id+"F26.wireOp",EDGE,"E106.98");var subQ1=sQuery(id+"F26.wireOp",EDGE,"E106.3");var subQ2=makeQuery(id+"F26.imprint","INTERSECT",VERTEX,{"derivedFrom":[subQ1,subQ0]});Q2=makeQuery(id+"F26.imprint","IMPRINT",FACE,{"disambiguationData":[TD([[makeQuery(id+"F26.imprint","IMPRINT",EDGE,{"disambiguationData":[TD([[subQ2,-1.0]])],"derivedFrom":subQ1}),-1.0]])]});}
            var Q3;
            {var subQ0=sQuery(id+"F26.wireOp",EDGE,"E106.97");var subQ1=sQuery(id+"F26.wireOp",EDGE,"E106.3");var subQ2=makeQuery(id+"F26.imprint","INTERSECT",VERTEX,{"derivedFrom":[subQ1,subQ0]});Q3=makeQuery(id+"F26.imprint","IMPRINT",FACE,{"disambiguationData":[TD([[makeQuery(id+"F26.imprint","IMPRINT",EDGE,{"disambiguationData":[TD([[subQ2,-1.0]])],"derivedFrom":subQ1}),-1.0]])]});}
            var Q4;
            {var subQ0=sQuery(id+"F26.wireOp",EDGE,"E106.97");var subQ1=sQuery(id+"F26.wireOp",EDGE,"E106.3");var subQ2=makeQuery(id+"F26.imprint","INTERSECT",VERTEX,{"derivedFrom":[subQ1,subQ0]});Q4=makeQuery(id+"F26.imprint","IMPRINT",FACE,{"disambiguationData":[TD([[makeQuery(id+"F26.imprint","IMPRINT",EDGE,{"disambiguationData":[TD([[subQ2,-1.0]])],"derivedFrom":subQ1}),1.0]])]});}
            var Q5;
            {var subQ7=sQuery(id+"F26.wireOp",EDGE,"E106.34");var subQ8=sQuery(id+"F26.wireOp",EDGE,"E106.10");var subQ9=makeQuery(id+"F26.imprint","INTERSECT",VERTEX,{"derivedFrom":[subQ8,subQ7]});Q5=makeQuery(id+"F26.imprint","IMPRINT",FACE,{"disambiguationData":[TD([[makeQuery(id+"F26.imprint","IMPRINT",EDGE,{"disambiguationData":[TD([[subQ9,-1.0]])],"derivedFrom":subQ8}),-1.0]])]});}
            var Q6;
            {var subQ0=sQuery(id+"F26.wireOp",EDGE,"E106.93");var subQ1=sQuery(id+"F26.wireOp",EDGE,"E106.3");var subQ2=makeQuery(id+"F26.imprint","INTERSECT",VERTEX,{"derivedFrom":[subQ1,subQ0]});Q6=makeQuery(id+"F26.imprint","IMPRINT",FACE,{"disambiguationData":[TD([[makeQuery(id+"F26.imprint","IMPRINT",EDGE,{"disambiguationData":[TD([[subQ2,-1.0]])],"derivedFrom":subQ1}),-1.0]])]});}
            var Q7;
            {var subQ0=sQuery(id+"F26.wireOp",EDGE,"E106.93");var subQ1=sQuery(id+"F26.wireOp",EDGE,"E106.3");var subQ2=makeQuery(id+"F26.imprint","INTERSECT",VERTEX,{"derivedFrom":[subQ1,subQ0]});Q7=makeQuery(id+"F26.imprint","IMPRINT",FACE,{"disambiguationData":[TD([[makeQuery(id+"F26.imprint","IMPRINT",EDGE,{"disambiguationData":[TD([[subQ2,-1.0]])],"derivedFrom":subQ1}),1.0]])]});}
            extrude(context, id + "F27", {"entities" : qUnion([Q0, Q1, Q2, Q3, Q4, Q5, Q6, Q7]), "operationType" : NewBodyOperationType.ADD, "depth" : 10 * mm});
        }
        {
            var Q0;
            Q0=makeQuery(id+"F27.opExtrude","SWEPT_EDGE",EDGE,{"disambiguationData":[OSD([sQuery(id+"F26.wireOp",EDGE,"E106.93"),sQuery(id+"F26.wireOp",EDGE,"E108"),sQuery(id+"F26.wireOp",EDGE,"E109")])]});
            var Q1;
            Q1=makeQuery(id+"F27.opExtrude","SWEPT_EDGE",EDGE,{"disambiguationData":[OSD([sQuery(id+"F26.wireOp",EDGE,"E106.97"),sQuery(id+"F26.wireOp",EDGE,"E109")])]});
            var Q2;
            Q2=makeQuery(id+"F27.boolean.opBoolean","MERGE",EDGE,{"derivedFrom":[makeQuery(id+"F24.opExtrude","SWEPT_EDGE",EDGE,{"disambiguationData":[OSD([sQuery(id+"F23.wireOp",EDGE,"E71.4"),sQuery(id+"F23.wireOp",EDGE,"E89")])]}),makeQuery(id+"F27.opExtrude","SWEPT_EDGE",EDGE,{"disambiguationData":[OSD([sQuery(id+"F26.wireOp",EDGE,"E106.4"),sQuery(id+"F26.wireOp",EDGE,"E106.98")])]})]});
            var Q3;
            Q3=makeQuery(id+"F27.boolean.opBoolean","MERGE",EDGE,{"derivedFrom":[makeQuery(id+"F24.opExtrude","SWEPT_EDGE",EDGE,{"disambiguationData":[OSD([sQuery(id+"F23.wireOp",EDGE,"E71.4"),sQuery(id+"F23.wireOp",EDGE,"E91")])]}),makeQuery(id+"F27.opExtrude","SWEPT_EDGE",EDGE,{"disambiguationData":[OSD([sQuery(id+"F26.wireOp",EDGE,"E106.4"),sQuery(id+"F26.wireOp",EDGE,"E106.100")])]})]});
            var Q4;
            Q4=makeQuery(id+"F27.opExtrude","CAP_EDGE",EDGE,{"disambiguationData":[OSD([sQuery(id+"F26.wireOp",EDGE,"E106.4")])],"isStart":false});
            fillet(context, id + "F28", {"entities" : qUnion([Q0, Q1, Q2, Q3, Q4]), "radius" : 2 * mm, "tangentPropagation" : true, "allowEdgeOverflow" : false});
        }
        {
            var Q0;
            {var subQ0=sQuery(id+"F23.wireOp",EDGE,"E71.4");Q0=makeQuery(id+"F27.boolean.opBoolean","MERGE",FACE,{"derivedFrom":[makeQuery(id+"F24.boolean.opBoolean","MERGE",FACE,{"derivedFrom":[makeQuery(id+"F1.opExtrude","SWEPT_FACE",FACE,{"disambiguationData":[OSD([sQuery(id+"F0.wireOp",EDGE,"E1.1")])]}),makeQuery(id+"F24.opExtrude","SWEPT_FACE",FACE,{"disambiguationData":[OSD([subQ0]),TDD([makeQuery(id+"F23.imprint","IMPRINT",EDGE,{"disambiguationData":[TD([[makeQuery(id+"F23.imprint","INTERSECT",VERTEX,{"derivedFrom":[subQ0,sQuery(id+"F23.wireOp",EDGE,"E88")]}),1.0]])],"derivedFrom":subQ0})])]}),makeQuery(id+"F24.opExtrude","SWEPT_FACE",FACE,{"disambiguationData":[OSD([subQ0]),TDD([makeQuery(id+"F23.imprint","IMPRINT",EDGE,{"disambiguationData":[TD([[makeQuery(id+"F23.imprint","INTERSECT",VERTEX,{"derivedFrom":[subQ0,sQuery(id+"F23.wireOp",EDGE,"E84")]}),-1.0]])],"derivedFrom":subQ0})])]})]}),makeQuery(id+"F27.opExtrude","SWEPT_FACE",FACE,{"disambiguationData":[OSD([sQuery(id+"F26.wireOp",EDGE,"E106.4")])]})]});}
            var sketch = newSketch(context, id + "F29", { "sketchPlane" : qUnion([Q0])});
            skCircle(sketch, "E110", {"center": v(61.23, 10.9) * mm, "radius": 3 * mm});
            skPoint(sketch, "E110.centerSnap0", {"position": v(66, 10.9) * mm});
            skCircle(sketch, "E111.0.1.0", {"center": v(61.23, 19.2) * mm, "radius": 3 * mm});
            skCircle(sketch, "E111.0.2.0", {"center": v(61.23, 27.5) * mm, "radius": 3 * mm});
            skLineSegment(sketch, "E111.direction1", {"start": v(61.23, 10.9) * mm, "end": v(86.23, 10.9) * mm, "construction": true});
            skLineSegment(sketch, "E111.direction2", {"start": v(61.23, 10.9) * mm, "end": v(61.23, 19.2) * mm, "construction": true});
            skCircle(sketch, "E112.0.1.0", {"center": v(61.23, 2.6) * mm, "radius": 3 * mm});
            skCircle(sketch, "E112.0.2.0", {"center": v(61.23, -5.7) * mm, "radius": 3 * mm});
            skLineSegment(sketch, "E112.direction2", {"start": v(61.23, 10.9) * mm, "end": v(61.23, 2.6) * mm, "construction": true});
            skCircle(sketch, "E113", {"center": v(27.6, 35.15) * mm, "radius": 2 * mm});
            skPoint(sketch, "E113.centerSnap0", {"position": v(31.7, 38.9) * mm});
            skCircle(sketch, "E114.1.0.0", {"center": v(35.6, 35.15) * mm, "radius": 2 * mm});
            skCircle(sketch, "E114.2.0.0", {"center": v(43.6, 35.15) * mm, "radius": 2 * mm});
            skLineSegment(sketch, "E114.direction1", {"start": v(27.6, 35.15) * mm, "end": v(35.6, 35.15) * mm, "construction": true});
            skCircle(sketch, "E115.1.0.0", {"center": v(19.6, 35.15) * mm, "radius": 2 * mm});
            skCircle(sketch, "E115.2.0.0", {"center": v(11.6, 35.15) * mm, "radius": 2 * mm});
            skLineSegment(sketch, "E115.direction1", {"start": v(27.6, 35.15) * mm, "end": v(19.6, 35.15) * mm, "construction": true});
            skCircle(sketch, "E116", {"center": v(27.67, -13.39) * mm, "radius": 2 * mm});
            skCircle(sketch, "E117.1.0.0", {"center": v(35.67, -13.39) * mm, "radius": 2 * mm});
            skCircle(sketch, "E117.2.0.0", {"center": v(43.67, -13.39) * mm, "radius": 2 * mm});
            skCircle(sketch, "E118.1.0.0", {"center": v(19.67, -13.39) * mm, "radius": 2 * mm});
            skCircle(sketch, "E118.2.0.0", {"center": v(11.67, -13.39) * mm, "radius": 2 * mm});
            skPoint(sketch, "E119.end.orphan", {"position": v(0, 31.9) * mm});
            skPoint(sketch, "E120.start.orphan", {"position": v(0, -10.1) * mm});
            skSolve(sketch);
        }
        {
            var Q0;
            Q0=makeQuery(id+"F29.imprint","IMPRINT",FACE,{"disambiguationData":[TD([[makeQuery(id+"F29.imprint","IMPRINT",EDGE,{"derivedFrom":sQuery(id+"F29.wireOp",EDGE,"E115.1.0.0")}),1.0]])]});
            var Q1;
            Q1=makeQuery(id+"F29.imprint","IMPRINT",FACE,{"disambiguationData":[TD([[makeQuery(id+"F29.imprint","IMPRINT",EDGE,{"derivedFrom":sQuery(id+"F29.wireOp",EDGE,"E115.2.0.0")}),1.0]])]});
            var Q2;
            Q2=makeQuery(id+"F29.imprint","IMPRINT",FACE,{"disambiguationData":[TD([[makeQuery(id+"F29.imprint","IMPRINT",EDGE,{"derivedFrom":sQuery(id+"F29.wireOp",EDGE,"E113")}),1.0]])]});
            var Q3;
            Q3=makeQuery(id+"F29.imprint","IMPRINT",FACE,{"disambiguationData":[TD([[makeQuery(id+"F29.imprint","IMPRINT",EDGE,{"derivedFrom":sQuery(id+"F29.wireOp",EDGE,"E114.1.0.0")}),1.0]])]});
            var Q4;
            Q4=makeQuery(id+"F29.imprint","IMPRINT",FACE,{"disambiguationData":[TD([[makeQuery(id+"F29.imprint","IMPRINT",EDGE,{"derivedFrom":sQuery(id+"F29.wireOp",EDGE,"E114.2.0.0")}),1.0]])]});
            var Q5;
            Q5=makeQuery(id+"F29.imprint","IMPRINT",FACE,{"disambiguationData":[TD([[makeQuery(id+"F29.imprint","IMPRINT",EDGE,{"derivedFrom":sQuery(id+"F29.wireOp",EDGE,"E111.0.2.0")}),1.0]])]});
            var Q6;
            Q6=makeQuery(id+"F29.imprint","IMPRINT",FACE,{"disambiguationData":[TD([[makeQuery(id+"F29.imprint","IMPRINT",EDGE,{"derivedFrom":sQuery(id+"F29.wireOp",EDGE,"E111.0.1.0")}),1.0]])]});
            var Q7;
            Q7=makeQuery(id+"F29.imprint","IMPRINT",FACE,{"disambiguationData":[TD([[makeQuery(id+"F29.imprint","IMPRINT",EDGE,{"derivedFrom":sQuery(id+"F29.wireOp",EDGE,"E110")}),1.0]])]});
            var Q8;
            Q8=makeQuery(id+"F29.imprint","IMPRINT",FACE,{"disambiguationData":[TD([[makeQuery(id+"F29.imprint","IMPRINT",EDGE,{"derivedFrom":sQuery(id+"F29.wireOp",EDGE,"E112.0.1.0")}),1.0]])]});
            var Q9;
            Q9=makeQuery(id+"F29.imprint","IMPRINT",FACE,{"disambiguationData":[TD([[makeQuery(id+"F29.imprint","IMPRINT",EDGE,{"derivedFrom":sQuery(id+"F29.wireOp",EDGE,"E112.0.2.0")}),1.0]])]});
            var Q10;
            Q10=makeQuery(id+"F29.imprint","IMPRINT",FACE,{"disambiguationData":[TD([[makeQuery(id+"F29.imprint","IMPRINT",EDGE,{"derivedFrom":sQuery(id+"F29.wireOp",EDGE,"E117.2.0.0")}),1.0]])]});
            var Q11;
            Q11=makeQuery(id+"F29.imprint","IMPRINT",FACE,{"disambiguationData":[TD([[makeQuery(id+"F29.imprint","IMPRINT",EDGE,{"derivedFrom":sQuery(id+"F29.wireOp",EDGE,"E117.1.0.0")}),1.0]])]});
            var Q12;
            Q12=makeQuery(id+"F29.imprint","IMPRINT",FACE,{"disambiguationData":[TD([[makeQuery(id+"F29.imprint","IMPRINT",EDGE,{"derivedFrom":sQuery(id+"F29.wireOp",EDGE,"E116")}),1.0]])]});
            var Q13;
            Q13=makeQuery(id+"F29.imprint","IMPRINT",FACE,{"disambiguationData":[TD([[makeQuery(id+"F29.imprint","IMPRINT",EDGE,{"derivedFrom":sQuery(id+"F29.wireOp",EDGE,"E118.1.0.0")}),1.0]])]});
            var Q14;
            Q14=makeQuery(id+"F29.imprint","IMPRINT",FACE,{"disambiguationData":[TD([[makeQuery(id+"F29.imprint","IMPRINT",EDGE,{"derivedFrom":sQuery(id+"F29.wireOp",EDGE,"E118.2.0.0")}),1.0]])]});
            var Q15;
            {var subQ0=sQuery(id+"F25.wireOp",EDGE,"E97");var subQ1=sQuery(id+"F25.wireOp",EDGE,"E94");var subQ2=makeQuery(id+"F25.imprint","INTERSECT",VERTEX,{"derivedFrom":[subQ1,subQ0]});Q15=makeQuery(id+"F25.imprint","IMPRINT",FACE,{"disambiguationData":[TD([[makeQuery(id+"F25.imprint","IMPRINT",EDGE,{"disambiguationData":[TD([[subQ2,-1.0]])],"derivedFrom":subQ1}),1.0]])]});}
            var Q16;
            {var subQ0=sQuery(id+"F25.wireOp",EDGE,"E97");var subQ1=sQuery(id+"F25.wireOp",EDGE,"E94");var subQ2=makeQuery(id+"F25.imprint","INTERSECT",VERTEX,{"derivedFrom":[subQ1,subQ0]});Q16=makeQuery(id+"F25.imprint","IMPRINT",FACE,{"disambiguationData":[TD([[makeQuery(id+"F25.imprint","IMPRINT",EDGE,{"disambiguationData":[TD([[subQ2,-1.0]])],"derivedFrom":subQ1}),-1.0]])]});}
            var Q17;
            {var subQ0=sQuery(id+"F25.wireOp",EDGE,"E95");var subQ1=sQuery(id+"F25.wireOp",EDGE,"E94");var subQ2=makeQuery(id+"F25.imprint","INTERSECT",VERTEX,{"derivedFrom":[subQ1,subQ0]});Q17=makeQuery(id+"F25.imprint","IMPRINT",FACE,{"disambiguationData":[TD([[makeQuery(id+"F25.imprint","IMPRINT",EDGE,{"disambiguationData":[TD([[subQ2,1.0]])],"derivedFrom":subQ1}),1.0]])]});}
            var Q18;
            {var subQ0=sQuery(id+"F25.wireOp",EDGE,"E95");var subQ1=sQuery(id+"F25.wireOp",EDGE,"E94");var subQ2=makeQuery(id+"F25.imprint","INTERSECT",VERTEX,{"derivedFrom":[subQ1,subQ0]});Q18=makeQuery(id+"F25.imprint","IMPRINT",FACE,{"disambiguationData":[TD([[makeQuery(id+"F25.imprint","IMPRINT",EDGE,{"disambiguationData":[TD([[subQ2,1.0]])],"derivedFrom":subQ1}),-1.0]])]});}
            var Q19;
            {var subQ0=sQuery(id+"F25.wireOp",EDGE,"E96");var subQ1=sQuery(id+"F25.wireOp",EDGE,"E95");var subQ2=makeQuery(id+"F25.imprint","INTERSECT",VERTEX,{"derivedFrom":[subQ1,subQ0]});Q19=makeQuery(id+"F25.imprint","IMPRINT",FACE,{"disambiguationData":[TD([[makeQuery(id+"F25.imprint","IMPRINT",EDGE,{"disambiguationData":[TD([[subQ2,1.0]])],"derivedFrom":subQ1}),1.0]])]});}
            var Q20;
            {var subQ0=sQuery(id+"F25.wireOp",EDGE,"E96");var subQ1=sQuery(id+"F25.wireOp",EDGE,"E95");var subQ2=makeQuery(id+"F25.imprint","INTERSECT",VERTEX,{"derivedFrom":[subQ1,subQ0]});Q20=makeQuery(id+"F25.imprint","IMPRINT",FACE,{"disambiguationData":[TD([[makeQuery(id+"F25.imprint","IMPRINT",EDGE,{"disambiguationData":[TD([[subQ2,1.0]])],"derivedFrom":subQ1}),-1.0]])]});}
            var Q21;
            {var subQ0=sQuery(id+"F25.wireOp",EDGE,"E97");var subQ1=sQuery(id+"F25.wireOp",EDGE,"E96");var subQ2=makeQuery(id+"F25.imprint","INTERSECT",VERTEX,{"derivedFrom":[subQ1,subQ0]});Q21=makeQuery(id+"F25.imprint","IMPRINT",FACE,{"disambiguationData":[TD([[makeQuery(id+"F25.imprint","IMPRINT",EDGE,{"disambiguationData":[TD([[subQ2,1.0]])],"derivedFrom":subQ1}),1.0]])]});}
            var Q22;
            {var subQ0=sQuery(id+"F25.wireOp",EDGE,"E97");var subQ1=sQuery(id+"F25.wireOp",EDGE,"E96");var subQ2=makeQuery(id+"F25.imprint","INTERSECT",VERTEX,{"derivedFrom":[subQ1,subQ0]});Q22=makeQuery(id+"F25.imprint","IMPRINT",FACE,{"disambiguationData":[TD([[makeQuery(id+"F25.imprint","IMPRINT",EDGE,{"disambiguationData":[TD([[subQ2,1.0]])],"derivedFrom":subQ1}),-1.0]])]});}
            extrude(context, id + "F30", {"entities" : qUnion([Q0, Q1, Q2, Q3, Q4, Q5, Q6, Q7, Q8, Q9, Q10, Q11, Q12, Q13, Q14, Q15, Q16, Q17, Q18, Q19, Q20, Q21, Q22]), "operationType" : NewBodyOperationType.REMOVE, "oppositeDirection" : true, "depth" : 8 * mm});
        }
        {
            var Q0;
            Q0=makeQuery(id+"F27.boolean.opBoolean","MERGE",FACE,{"derivedFrom":[makeQuery(id+"F24.opExtrude","SWEPT_FACE",FACE,{"disambiguationData":[OSD([sQuery(id+"F23.wireOp",EDGE,"E89")])]}),makeQuery(id+"F27.opExtrude","SWEPT_FACE",FACE,{"disambiguationData":[OSD([sQuery(id+"F26.wireOp",EDGE,"E106.98")])]})]});
            var sketch = newSketch(context, id + "F31", { "sketchPlane" : qUnion([Q0])});
            skLineSegment(sketch, "E121.0", {"start": v(29.9, 66) * mm, "end": v(29.9, 0) * mm});
            skLineSegment(sketch, "E121.1", {"start": v(35.9, 0) * mm, "end": v(35.9, 66) * mm});
            skLineSegment(sketch, "E121.2", {"start": v(29.9, 66) * mm, "end": v(35.9, 66) * mm});
            skLineSegment(sketch, "E121.3", {"start": v(31.36, 0) * mm, "end": v(35.9, 0) * mm});
            skLineSegment(sketch, "E121.4", {"start": v(29.9, 0) * mm, "end": v(31.36, 0) * mm});
            skLineSegment(sketch, "E122", {"start": v(32.9, 49.5) * mm, "end": v(32.9, 66) * mm});
            skLineSegment(sketch, "E123", {"start": v(32.9, 49.5) * mm, "end": v(29.9, 49.5) * mm});
            skLineSegment(sketch, "E124", {"start": v(32.9, 7.57) * mm, "end": v(29.9, 7.57) * mm});
            skLineSegment(sketch, "E125", {"start": v(32.9, 49.5) * mm, "end": v(34.26, 49.5) * mm});
            skLineSegment(sketch, "E126", {"start": v(34.3, 7.55) * mm, "end": v(32.9, 7.57) * mm});
            skLineSegment(sketch, "E127.trimOffspring", {"start": v(32.9, 7.57) * mm, "end": v(32.9, 0) * mm});
            skPoint(sketch, "E128.end.orphan", {"position": v(32.9, 16.5) * mm});
            skPoint(sketch, "E129.orphan", {"position": v(32.9, 33) * mm});
            skPoint(sketch, "E130.orphan", {"position": v(29.9, 33) * mm});
            skPoint(sketch, "E131.orphan", {"position": v(35.9, 33) * mm});
            skPoint(sketch, "E132.end.orphan", {"position": v(34.26, 7.57) * mm});
            skLineSegment(sketch, "E133", {"start": v(34.3, 7.55) * mm, "end": v(34.26, 49.5) * mm});
            skLineSegment(sketch, "E134", {"start": v(34.3, 7.55) * mm, "end": v(29.9, 7.57) * mm});
            skSolve(sketch);
        }
        {
            var Q0;
            {var subQ6=sQuery(id+"F31.wireOp",EDGE,"E123");Q0=makeQuery(id+"F31.imprint","IMPRINT",FACE,{"disambiguationData":[TD([[makeQuery(id+"F31.imprint","IMPRINT",EDGE,{"derivedFrom":subQ6}),1.0]])]});}
            extrude(context, id + "F32", {"entities" : qUnion([Q0]), "operationType" : NewBodyOperationType.REMOVE, "oppositeDirection" : true, "depth" : 64.1 * mm});
        }
        {
            var Q0;
            Q0=makeQuery(id+"F1.opExtrude","SWEPT_FACE",FACE,{"disambiguationData":[OSD([sQuery(id+"F0.wireOp",EDGE,"E48")])]});
            var sketch = newSketch(context, id + "F33", { "sketchPlane" : qUnion([Q0])});
            skLineSegment(sketch, "E135.0", {"start": v(-16.1, -2) * mm, "end": v(-34.1, -2) * mm});
            skLineSegment(sketch, "E135.1", {"start": v(-16.1, -13) * mm, "end": v(-16.1, -2) * mm});
            skLineSegment(sketch, "E135.2", {"start": v(-34.1, -13) * mm, "end": v(-16.1, -13) * mm});
            skLineSegment(sketch, "E135.3", {"start": v(-34.1, -2) * mm, "end": v(-34.1, -13) * mm});
            skLineSegment(sketch, "E136.0", {"start": v(33.9, -2) * mm, "end": v(12.9, -2) * mm});
            skLineSegment(sketch, "E136.1", {"start": v(33.9, -13) * mm, "end": v(33.9, -2) * mm});
            skLineSegment(sketch, "E136.2", {"start": v(12.9, -13) * mm, "end": v(33.9, -13) * mm});
            skLineSegment(sketch, "E136.3", {"start": v(12.9, -2) * mm, "end": v(12.9, -13) * mm});
            skCircle(sketch, "E137", {"center": v(-25.1, -7.5) * mm, "radius": 3 * mm});
            skPoint(sketch, "E137.centerSnap0", {"position": v(-25.1, -2) * mm});
            skPoint(sketch, "E137.centerSnap1", {"position": v(-34.1, -7.5) * mm});
            skCircle(sketch, "E138", {"center": v(23.4, -7.5) * mm, "radius": 3 * mm});
            skPoint(sketch, "E138.centerSnap0", {"position": v(23.4, -2) * mm});
            skPoint(sketch, "E138.centerSnap1", {"position": v(12.9, -7.5) * mm});
            skSolve(sketch);
        }
        {
            var Q0;
            Q0=makeQuery(id+"F33.imprint","IMPRINT",FACE,{"disambiguationData":[TD([[makeQuery(id+"F33.imprint","IMPRINT",EDGE,{"derivedFrom":sQuery(id+"F33.wireOp",EDGE,"E137")}),1.0]])]});
            var Q1;
            Q1=makeQuery(id+"F33.imprint","IMPRINT",FACE,{"disambiguationData":[TD([[makeQuery(id+"F33.imprint","IMPRINT",EDGE,{"derivedFrom":sQuery(id+"F33.wireOp",EDGE,"E138")}),1.0]])]});
            extrude(context, id + "F34", {"entities" : qUnion([Q0, Q1]), "operationType" : NewBodyOperationType.REMOVE, "oppositeDirection" : true, "depth" : 8 * mm});
        }
        {
            var Q0;
            Q0=makeQuery(id+"F33.imprint","IMPRINT",FACE,{"disambiguationData":[TD([[makeQuery(id+"F33.imprint","IMPRINT",EDGE,{"derivedFrom":sQuery(id+"F33.wireOp",EDGE,"E135.0")}),1.0]])]});
            var Q1;
            Q1=makeQuery(id+"F33.imprint","IMPRINT",FACE,{"disambiguationData":[TD([[makeQuery(id+"F33.imprint","IMPRINT",EDGE,{"derivedFrom":sQuery(id+"F33.wireOp",EDGE,"E136.0")}),1.0]])]});
            extrude(context, id + "F35", {"entities" : qUnion([Q0, Q1]), "operationType" : NewBodyOperationType.REMOVE, "oppositeDirection" : true, "depth" : 1 * mm});
        }
        {
            var Q0;
            Q0=makeQuery(id+"F23.imprint","IMPRINT",FACE,{"disambiguationData":[TD([[makeQuery(id+"F23.imprint","IMPRINT",EDGE,{"derivedFrom":sQuery(id+"F23.wireOp",EDGE,"E92")}),1.0]])]});
            extrude(context, id + "F36", {"entities" : qUnion([Q0]), "operationType" : NewBodyOperationType.ADD, "endBound" : BoundingType.UP_TO_NEXT, "oppositeDirection" : true, "depth" : 1 * mm});
        }
        {
            var Q0;
            Q0=makeQuery(id+"F23.imprint","IMPRINT",FACE,{"disambiguationData":[TD([[makeQuery(id+"F23.imprint","IMPRINT",EDGE,{"derivedFrom":sQuery(id+"F23.wireOp",EDGE,"E93")}),1.0]])]});
            extrude(context, id + "F37", {"entities" : qUnion([Q0]), "operationType" : NewBodyOperationType.ADD, "endBound" : BoundingType.UP_TO_NEXT, "oppositeDirection" : true, "depth" : 1 * mm});
        }
        {
            var Q0;
            {var subQ0=sQuery(id+"F31.wireOp",EDGE,"E126");var subQ1=sQuery(id+"F31.wireOp",EDGE,"E133");Q0=makeQuery(id+"F32.boolean.opBoolean","COPY",EDGE,{"disambiguationData":[TD([makeQuery(id+"F24.opExtrude","SWEPT_FACE",FACE,{"disambiguationData":[OSD([sQuery(id+"F23.wireOp",EDGE,"E84")])]})])],"derivedFrom":makeQuery(id+"F32.opExtrude","SWEPT_EDGE",EDGE,{"disambiguationData":[OSD([subQ0,subQ1,sQuery(id+"F31.wireOp",EDGE,"E134")])]})});}
            var Q1;
            {var subQ0=sQuery(id+"F31.wireOp",EDGE,"E125");var subQ1=sQuery(id+"F31.wireOp",EDGE,"E133");Q1=makeQuery(id+"F32.boolean.opBoolean","COPY",EDGE,{"disambiguationData":[TD([makeQuery(id+"F24.opExtrude","SWEPT_FACE",FACE,{"disambiguationData":[OSD([sQuery(id+"F23.wireOp",EDGE,"E84")])]})])],"derivedFrom":makeQuery(id+"F32.opExtrude","SWEPT_EDGE",EDGE,{"disambiguationData":[OSD([subQ0,subQ1])]})});}
            var Q2;
            {var subQ0=sQuery(id+"F31.wireOp",EDGE,"E126");var subQ1=sQuery(id+"F31.wireOp",EDGE,"E133");Q2=makeQuery(id+"F32.boolean.opBoolean","COPY",EDGE,{"disambiguationData":[TD([makeQuery(id+"F24.opExtrude","SWEPT_FACE",FACE,{"disambiguationData":[OSD([sQuery(id+"F23.wireOp",EDGE,"E88")])]})])],"derivedFrom":makeQuery(id+"F32.opExtrude","SWEPT_EDGE",EDGE,{"disambiguationData":[OSD([subQ0,subQ1,sQuery(id+"F31.wireOp",EDGE,"E134")])]})});}
            fillet(context, id + "F38", {"entities" : qUnion([Q0, Q1, Q2]), "radius" : 5 * mm, "tangentPropagation" : true, "allowEdgeOverflow" : false});
        }
        {
            var Q0;
            {var subQ0=sQuery(id+"F31.wireOp",EDGE,"E125");var subQ1=sQuery(id+"F31.wireOp",EDGE,"E133");Q0=makeQuery(id+"F32.boolean.opBoolean","COPY",EDGE,{"disambiguationData":[TD([makeQuery(id+"F24.opExtrude","SWEPT_FACE",FACE,{"disambiguationData":[OSD([sQuery(id+"F23.wireOp",EDGE,"E88")])]})])],"derivedFrom":makeQuery(id+"F32.opExtrude","SWEPT_EDGE",EDGE,{"disambiguationData":[OSD([subQ0,subQ1])]})});}
            var Q1;
            Q1=makeQuery(id+"F27.opExtrude","CAP_EDGE",EDGE,{"disambiguationData":[OSD([sQuery(id+"F26.wireOp",EDGE,"E106.90"),sQuery(id+"F26.wireOp",EDGE,"E106.92")])],"isStart":false});
            var Q2;
            Q2=makeQuery(id+"F27.opExtrude","CAP_EDGE",EDGE,{"disambiguationData":[OSD([sQuery(id+"F26.wireOp",EDGE,"E106.81"),sQuery(id+"F26.wireOp",EDGE,"E106.96")])],"isStart":false});
            var Q3;
            {var subQ0=sQuery(id+"F31.wireOp",EDGE,"E123");Q3=makeQuery(id+"F32.boolean.opBoolean","COPY",EDGE,{"disambiguationData":[TD([makeQuery(id+"F24.opExtrude","SWEPT_FACE",FACE,{"disambiguationData":[OSD([sQuery(id+"F23.wireOp",EDGE,"E88")])]})])],"derivedFrom":makeQuery(id+"F32.opExtrude","SWEPT_EDGE",EDGE,{"disambiguationData":[OSD([sQuery(id+"F31.wireOp",EDGE,"E121.0"),subQ0])]})});}
            var Q4;
            {var subQ2=sQuery(id+"F26.wireOp",EDGE,"E106.96");var subQ4=sQuery(id+"F26.wireOp",EDGE,"E106.92");var subQ5=sQuery(id+"F26.wireOp",EDGE,"E106.90");var subQ6=sQuery(id+"F26.wireOp",EDGE,"E106.81");var subQ9=makeQuery(id+"F24.opExtrude","SWEPT_FACE",FACE,{"disambiguationData":[OSD([sQuery(id+"F23.wireOp",EDGE,"E84")])]});var subQ11=sQuery(id+"F31.wireOp",EDGE,"E125");var subQ13=sQuery(id+"F31.wireOp",EDGE,"E133");Q4=makeQuery(id+"F38.opFillet","BLEND_EDGE",EDGE,{"blendedFrom":[makeQuery(id+"F32.boolean.opBoolean","COPY",EDGE,{"disambiguationData":[TD([subQ9])],"derivedFrom":makeQuery(id+"F32.opExtrude","SWEPT_EDGE",EDGE,{"disambiguationData":[OSD([subQ11,subQ13])]})}),makeQuery(id+"F32.boolean.opBoolean","SPLIT",FACE,{"disambiguationData":[TD([makeQuery(id+"F30.boolean.opBoolean","COPY",FACE,{"derivedFrom":makeQuery(id+"F30.opExtrude","SWEPT_FACE",FACE,{"disambiguationData":[OSD([sQuery(id+"F25.wireOp",EDGE,"E103")])]})})])],"derivedFrom":makeQuery(id+"F27.boolean.opBoolean","MERGE",FACE,{"derivedFrom":[makeQuery(id+"F24.boolean.opBoolean","MERGE",FACE,{"derivedFrom":[makeQuery(id+"F1.opExtrude","SWEPT_FACE",FACE,{"disambiguationData":[OSD([sQuery(id+"F0.wireOp",EDGE,"E0.left")])]}),makeQuery(id+"F24.opExtrude","SWEPT_FACE",FACE,{"disambiguationData":[OSD([sQuery(id+"F23.wireOp",EDGE,"E72"),sQuery(id+"F23.wireOp",EDGE,"E87")])]}),makeQuery(id+"F24.opExtrude","SWEPT_FACE",FACE,{"disambiguationData":[OSD([sQuery(id+"F23.wireOp",EDGE,"E81"),sQuery(id+"F23.wireOp",EDGE,"E83")])]})]}),makeQuery(id+"F27.opExtrude","SWEPT_FACE",FACE,{"disambiguationData":[OSD([subQ6,subQ2])]}),makeQuery(id+"F27.opExtrude","SWEPT_FACE",FACE,{"disambiguationData":[OSD([subQ5,subQ4])]})]})})],"blendedInto":[makeQuery(id+"F32.boolean.opBoolean","SPLIT",FACE,{"disambiguationData":[TD([makeQuery(id+"F30.boolean.opBoolean","COPY",FACE,{"derivedFrom":makeQuery(id+"F30.opExtrude","SWEPT_FACE",FACE,{"disambiguationData":[OSD([sQuery(id+"F25.wireOp",EDGE,"E103")])]})})])],"derivedFrom":makeQuery(id+"F27.boolean.opBoolean","MERGE",FACE,{"derivedFrom":[makeQuery(id+"F24.boolean.opBoolean","MERGE",FACE,{"derivedFrom":[makeQuery(id+"F1.opExtrude","SWEPT_FACE",FACE,{"disambiguationData":[OSD([sQuery(id+"F0.wireOp",EDGE,"E0.left")])]}),makeQuery(id+"F24.opExtrude","SWEPT_FACE",FACE,{"disambiguationData":[OSD([sQuery(id+"F23.wireOp",EDGE,"E72"),sQuery(id+"F23.wireOp",EDGE,"E87")])]}),makeQuery(id+"F24.opExtrude","SWEPT_FACE",FACE,{"disambiguationData":[OSD([sQuery(id+"F23.wireOp",EDGE,"E81"),sQuery(id+"F23.wireOp",EDGE,"E83")])]})]}),makeQuery(id+"F27.opExtrude","SWEPT_FACE",FACE,{"disambiguationData":[OSD([subQ6,subQ2])]}),makeQuery(id+"F27.opExtrude","SWEPT_FACE",FACE,{"disambiguationData":[OSD([subQ5,subQ4])]})]})})]});}
            var Q5;
            {var subQ0=sQuery(id+"F31.wireOp",EDGE,"E124");Q5=makeQuery(id+"F32.boolean.opBoolean","COPY",EDGE,{"disambiguationData":[TD([makeQuery(id+"F24.opExtrude","SWEPT_FACE",FACE,{"disambiguationData":[OSD([sQuery(id+"F23.wireOp",EDGE,"E84")])]})])],"derivedFrom":makeQuery(id+"F32.opExtrude","SWEPT_EDGE",EDGE,{"disambiguationData":[OSD([sQuery(id+"F31.wireOp",EDGE,"E121.0"),subQ0,sQuery(id+"F31.wireOp",EDGE,"E134")])]})});}
            var Q6;
            {var subQ0=sQuery(id+"F31.wireOp",EDGE,"E124");Q6=makeQuery(id+"F32.boolean.opBoolean","COPY",EDGE,{"disambiguationData":[TD([makeQuery(id+"F24.opExtrude","SWEPT_FACE",FACE,{"disambiguationData":[OSD([sQuery(id+"F23.wireOp",EDGE,"E88")])]})])],"derivedFrom":makeQuery(id+"F32.opExtrude","SWEPT_EDGE",EDGE,{"disambiguationData":[OSD([sQuery(id+"F31.wireOp",EDGE,"E121.0"),subQ0,sQuery(id+"F31.wireOp",EDGE,"E134")])]})});}
            fillet(context, id + "F39", {"entities" : qUnion([Q0, Q1, Q2, Q3, Q4, Q5, Q6]), "radius" : 2 * mm, "tangentPropagation" : true, "allowEdgeOverflow" : false});
        }
    });
